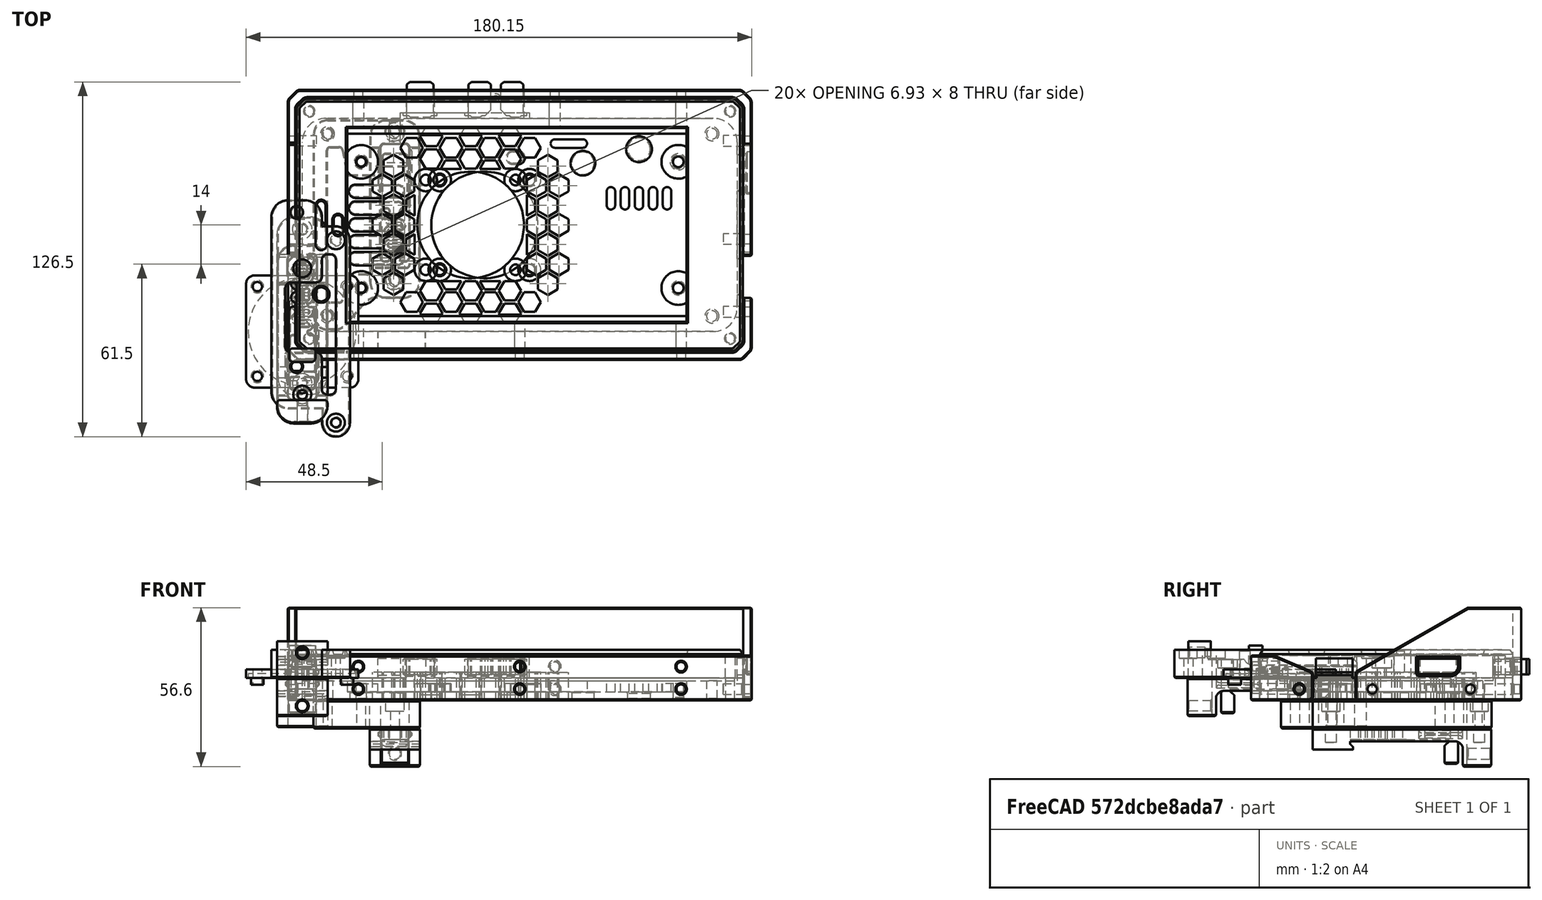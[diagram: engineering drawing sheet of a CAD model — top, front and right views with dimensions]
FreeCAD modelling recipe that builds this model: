
FCSTD DOCUMENT  (FreeCAD 0.19R24291 (Git))
Label: pixel-xl-navi-case-trim
License: Other
LicenseURL: GPL3
objects: Sketcher::SketchObject×56, PartDesign::Pocket×40, PartDesign::Chamfer×24, PartDesign::Pad×21, PartDesign::Fillet×18, Part::Box×16, PartDesign::Plane×12, Part::Feature×10, Part::MultiFuse×10, PartDesign::Body×9, Part::Chamfer×7, Part::Cylinder×6, Part::Cut×5, Part::Fillet×3, PartDesign::FeatureBase×2, Spreadsheet::Sheet×1, Mesh::Feature×1, Part::FeaturePython×1, Part::Extrusion×1
note: 344 computed .brp shape members not serialized (recipe doc carries the construction recipe); baked Part::Feature solids carry a one-line shape summary decoded from their .brp

FEATURE [Spreadsheet::Sheet] Spreadsheet  label="args"
  cells = A2=pixel width; B2(pixel_w)=155; A3=pixel heigh; B3(pixel_h)=76; A4=pixel thickness; B4(pixel_t)=8; A5=top screen offset; B5(screen_top_offset)=16; A6=bottom screen offset; B6(screen_bottom_offset)=17; A7=side screen offset; B7(screen_side_offset)=3.5; A8=power button offset; B8(button_power_offset)=37; A9=volume button offset; B9(button_volume_offset)=59; A10=power button width; B10(button_power_width)=10; A11=volume button width; B11(button_volume_width)=20; A12=screen width; B12(screen_width)=121; A13=screen heigh; B13(screen_heigh)=69; A14=pixel corner radius; B14(pixel_corner_radius)=8.5; A18=case thickness; B18(case_thickness)=10; A19=case width offset; B19(case_width_offset)=2; A20=case heigh offset; B20(case_heigh_offset)=7; A21=case corner radius; B21(case_corner_radius)=3; A23=front speaker offset; B23(front_speaker_offset)=5.75; A24=front speaker width; B24(front_speaker_width)=2; A25=front speaker heigh; B25(front_speaker_heigh)=16; A27=light sensor width; B27(light_sensor_width)=2; A28=light sensor heigh; B28(light_sensor_heigh)=6; A29=light sensor offset; B29(light_sensor_offset)=11.75; A31=camera x offset; B31(camera_x_offset)=6.75; A32=camera y offset; B32(camera_y_offset)=13.25; A33=camera radius; B33(camera_radius)=2; A35=speaker offset; B35(spekaer_offset)=14; A36=speaker width; B36(speaker_width)=11; A39=back thickness; B39(back_thickness)=8; A41=fan offset; B41(fan_offset)=65; C41=60; A43=wiring hole offset; B43(wiring_hole_offset)=120; A44=wiring hole radius; B44(wiring_hole_radius)=4; A46=sim slot offset; B46(sim_slot_offset)=28; A47=sim slot width; B47(sim_slot_width)=15; A49=headphone jack center offset; B49(headphone_jack_center_offset)=22; A50=headphone jack radius; B50(headphone_jack_radius)=5; A51=headphone_jack_width; B51(headphone_jack_width)=8; A53=sun visor heigh; B53(sun_visor_heigh)=15; A54=sun visor ramp width; B54(sun_visor_ramp_width)=40
FEATURE [Sketcher::SketchObject] Sketch
  FullyConstrained = true
  MapMode = 5
  Support = -> [XY_Plane]
  expr: Constraints[8] = <<args>>.case_heigh_offset
  expr: Constraints[9] = <<args>>.case_width_offset
  expr: Constraints[10] = <<args>>.pixel_h + <<args>>.case_heigh_offset
  expr: Constraints[11] = <<args>>.pixel_w + <<args>>.case_width_offset
  sketch-geometry (4):
    g0: LineSegment StartX=-2 StartY=-7 StartZ=0 EndX=157 EndY=-7 EndZ=0
    g1: LineSegment StartX=157 StartY=-7 StartZ=0 EndX=157 EndY=83 EndZ=0
    g2: LineSegment StartX=157 StartY=83 StartZ=0 EndX=-2 EndY=83 EndZ=0
    g3: LineSegment StartX=-2 StartY=83 StartZ=0 EndX=-2 EndY=-7 EndZ=0
  constraints (12):
    c: Coincident(g0,g1)
    c: Coincident(g1,g2)
    c: Coincident(g2,g3)
    c: Coincident(g3,g0)
    c: Horizontal(g0)
    c: Horizontal(g2)
    c: Vertical(g1)
    c: Vertical(g3)
    c: DistanceY(g0,g-1) = 7
    c: DistanceX(g0,g-1) = 2
    c: DistanceY(g-1,g2) = 83
    c: DistanceX(g-1,g1) = 157
FEATURE [PartDesign::Pad] Pad
  Direction = (1,1,1)
  Length = 10
  Length2 = 100
  Profile = -> Sketch
  Type = 0
  expr: Length = <<args>>.case_thickness
FEATURE [PartDesign::Plane] DatumPlane  label="face-plane"
  AttachmentOffset = pos=(0,0,10) rot=(0,0,1;0rad)
  Length = 210.04
  MapMode = 5
  Placement = pos=(0,0,10) rot=(0,0,1;0rad)
  ResizeMode = 0
  Support = -> [XY_Plane]
  Width = 136.04
  expr: .AttachmentOffset.Base.z = <<args>>.case_thickness
FEATURE [Sketcher::SketchObject] Sketch001
  FullyConstrained = true
  MapMode = 5
  Placement = pos=(0,0,10) rot=(0,0,1;0rad)
  Support = -> [DatumPlane]
  expr: Constraints[8] = <<args>>.screen_top_offset
  expr: Constraints[9] = <<args>>.screen_side_offset
  expr: Constraints[10] = <<args>>.screen_width
  expr: Constraints[11] = <<args>>.screen_heigh
  sketch-geometry (4):
    g0: LineSegment StartX=16 StartY=72.5 StartZ=0 EndX=137 EndY=72.5 EndZ=0
    g1: LineSegment StartX=137 StartY=72.5 StartZ=0 EndX=137 EndY=3.5 EndZ=0
    g2: LineSegment StartX=137 StartY=3.5 StartZ=0 EndX=16 EndY=3.5 EndZ=0
    g3: LineSegment StartX=16 StartY=3.5 StartZ=0 EndX=16 EndY=72.5 EndZ=0
  constraints (12):
    c: Coincident(g0,g1)
    c: Coincident(g1,g2)
    c: Coincident(g2,g3)
    c: Coincident(g3,g0)
    c: Horizontal(g0)
    c: Horizontal(g2)
    c: Vertical(g1)
    c: Vertical(g3)
    c: DistanceX(g-1,g2) = 16
    c: DistanceY(g-1,g2) = 3.5
    c: DistanceX(g0,g0) = 121
    c: DistanceY(g1,g1) = 69
FEATURE [PartDesign::Pocket] Pocket
  BaseFeature = -> Pad
  Length = 5
  Length2 = 100
  Profile = -> Sketch001
  Type = 1
FEATURE [PartDesign::Plane] DatumPlane001  label="zero-plane"
  Length = 210.04
  MapMode = 5
  ResizeMode = 0
  Support = -> [XY_Plane]
  Width = 136.04
FEATURE [Sketcher::SketchObject] Sketch002
  FullyConstrained = true
  MapMode = 5
  Support = -> [DatumPlane001]
  expr: Constraints[9] = <<args>>.pixel_w
  expr: Constraints[10] = <<args>>.pixel_h
  sketch-geometry (4):
    g0: LineSegment StartX=0 StartY=0 StartZ=0 EndX=155 EndY=0 EndZ=0
    g1: LineSegment StartX=155 StartY=0 StartZ=0 EndX=155 EndY=76 EndZ=0
    g2: LineSegment StartX=155 StartY=76 StartZ=0 EndX=0 EndY=76 EndZ=0
    g3: LineSegment StartX=0 StartY=76 StartZ=0 EndX=0 EndY=0 EndZ=0
  constraints (11):
    c: Coincident(g0,g1)
    c: Coincident(g1,g2)
    c: Coincident(g2,g3)
    c: Coincident(g3,g0)
    c: Horizontal(g0)
    c: Horizontal(g2)
    c: Vertical(g1)
    c: Vertical(g3)
    c: Coincident(g0,g-1)
    c: DistanceX(g2,g2) = 155
    c: DistanceY(g1,g1) = 76
FEATURE [PartDesign::Pocket] Pocket001
  BaseFeature = -> Pocket
  Length = 8
  Length2 = 100
  Profile = -> Sketch002
  Reversed = true
  Type = 0
  expr: Length = <<args>>.case_thickness - 2
FEATURE [Sketcher::SketchObject] Sketch003
  FullyConstrained = true
  MapMode = 5
  Placement = pos=(0,0,10) rot=(0,0,1;0rad)
  Support = -> [DatumPlane]
  expr: Constraints[12] = <<args>>.camera_radius + 0.5
  expr: Constraints[13] = <<args>>.camera_x_offset
  expr: Constraints[14] = <<args>>.camera_y_offset
  expr: Constraints[17] = <<args>>.front_speaker_heigh - <<args>>.front_speaker_width
  expr: Constraints[22] = (<<args>>.pixel_h - <<args>>.light_sensor_heigh) / 2 + <<args>>.light_sensor_width / 2
  expr: Constraints[15] = <<args>>.front_speaker_offset + <<args>>.front_speaker_width / 2
  expr: Constraints[20] = <<args>>.light_sensor_offset + <<args>>.light_sensor_width / 2
  expr: Constraints[16] = (<<args>>.pixel_h - <<args>>.front_speaker_heigh) / 2 + <<args>>.front_speaker_width / 2
  expr: Constraints[18] = <<args>>.front_speaker_width / 2 + 0.5
  expr: Constraints[19] = <<args>>.light_sensor_width / 2 + 0.5
  expr: Constraints[21] = <<args>>.light_sensor_heigh - <<args>>.light_sensor_width
  sketch-geometry (9):
    g0: ArcOfCircle CenterX=6.75 CenterY=45 CenterZ=0 NormalX=0 NormalY=0 NormalZ=1 AngleXU=0 Radius=1.5 StartAngle=2e-16 EndAngle=3.14159
    g1: ArcOfCircle CenterX=6.75 CenterY=31 CenterZ=0 NormalX=0 NormalY=0 NormalZ=1 AngleXU=0 Radius=1.5 StartAngle=3.14159 EndAngle=6.28319
    g2: LineSegment StartX=5.25 StartY=45 StartZ=0 EndX=5.25 EndY=31 EndZ=0
    g3: LineSegment StartX=8.25 StartY=45 StartZ=0 EndX=8.25 EndY=31 EndZ=0
    g4: ArcOfCircle CenterX=12.75 CenterY=40 CenterZ=0 NormalX=0 NormalY=0 NormalZ=1 AngleXU=0 Radius=1.5 StartAngle=2.4e-15 EndAngle=3.14159
    g5: ArcOfCircle CenterX=12.75 CenterY=36 CenterZ=0 NormalX=0 NormalY=0 NormalZ=1 AngleXU=0 Radius=1.5 StartAngle=3.14159 EndAngle=6.28319
    g6: LineSegment StartX=11.25 StartY=40 StartZ=0 EndX=11.25 EndY=36 EndZ=0
    g7: LineSegment StartX=14.25 StartY=40 StartZ=0 EndX=14.25 EndY=36 EndZ=0
    g8: Circle CenterX=6.75 CenterY=13.25 CenterZ=0 NormalX=0 NormalY=0 NormalZ=1 AngleXU=0 Radius=2.5
  constraints (23):
    c: Tangent(g0,g3) = 1.5708
    c: Tangent(g0,g2) = -1.5708
    c: Tangent(g2,g1) = -1.5708
    c: Tangent(g3,g1) = 1.5708
    c: Vertical(g2)
    c: Equal(g0,g1)
    c: Tangent(g4,g7) = 1.5708
    c: Tangent(g4,g6) = -1.5708
    c: Tangent(g6,g5) = -1.5708
    c: Tangent(g7,g5) = 1.5708
    c: Vertical(g6)
    c: Equal(g4,g5)
    c: Radius(g8) = 2.5
    c: DistanceX(g-1,g8) = 6.75
    c: DistanceY(g-1,g8) = 13.25
    c: DistanceX(g-1,g1) = 6.75
    c: DistanceY(g-1,g1) = 31
    c: DistanceY(g1,g0) = 14
    c: Radius(g0) = 1.5
    c: Radius(g4) = 1.5
    c: DistanceX(g-1,g5) = 12.75
    c: DistanceY(g5,g4) = 4
    c: DistanceY(g-1,g5) = 36
FEATURE [PartDesign::Pocket] Pocket002
  BaseFeature = -> Pocket001
  Length = 5
  Length2 = 100
  Profile = -> Sketch003
  Type = 1
FEATURE [PartDesign::Plane] DatumPlane002  label="right-edge-plane"
  AttachmentOffset = pos=(0,0,-83) rot=(0,0,1;0rad)
  Length = 201.079
  MapMode = 5
  Placement = pos=(0,83,1.84e-14) rot=(1,0,0;1.5708rad)
  ResizeMode = 0
  Support = -> [XZ_Plane]
  Width = 69.0788
  expr: .AttachmentOffset.Base.z = -(<<args>>.pixel_h + <<args>>.case_heigh_offset)
FEATURE [Sketcher::SketchObject] Sketch007
  FullyConstrained = true
  MapMode = 5
  Placement = pos=(0,83,1.84e-14) rot=(1,0,0;1.5708rad)
  Support = -> [DatumPlane002]
  expr: Constraints[19] = <<args>>.button_power_offset
  expr: Constraints[18] = <<args>>.button_volume_offset
  expr: Constraints[17] = <<args>>.button_volume_width
  expr: Constraints[16] = <<args>>.button_power_width
  sketch-geometry (8):
    g0: LineSegment StartX=37 StartY=7 StartZ=0 EndX=47 EndY=7 EndZ=0
    g1: LineSegment StartX=47 StartY=7 StartZ=0 EndX=47 EndY=0 EndZ=0
    g2: LineSegment StartX=47 StartY=0 StartZ=0 EndX=37 EndY=0 EndZ=0
    g3: LineSegment StartX=37 StartY=0 StartZ=0 EndX=37 EndY=7 EndZ=0
    g4: LineSegment StartX=59 StartY=7 StartZ=0 EndX=79 EndY=7 EndZ=0
    g5: LineSegment StartX=79 StartY=7 StartZ=0 EndX=79 EndY=0 EndZ=0
    g6: LineSegment StartX=79 StartY=0 StartZ=0 EndX=59 EndY=0 EndZ=0
    g7: LineSegment StartX=59 StartY=0 StartZ=0 EndX=59 EndY=7 EndZ=0
  constraints (24):
    c: Coincident(g0,g1)
    c: Coincident(g1,g2)
    c: Coincident(g2,g3)
    c: Coincident(g3,g0)
    c: Horizontal(g0)
    c: Horizontal(g2)
    c: Vertical(g1)
    c: Vertical(g3)
    c: Coincident(g4,g5)
    c: Coincident(g5,g6)
    c: Coincident(g6,g7)
    c: Coincident(g7,g4)
    c: Horizontal(g4)
    c: Horizontal(g6)
    c: Vertical(g5)
    c: Vertical(g7)
    c: DistanceX(g2,g2) = 10
    c: DistanceX(g6,g6) = 20
    c: DistanceX(g-1,g6) = 59
    c: DistanceX(g-1,g2) = 37
    c: DistanceY(g-1,g2) = 0
    c: DistanceY(g-1,g6) = 0
    c: DistanceY(g3,g3) = 7
    c: DistanceY(g7,g7) = 7
FEATURE [PartDesign::Plane] DatumPlane003  label="bottom-edge-plane"
  AttachmentOffset = pos=(0,0,157) rot=(0,0,1;0rad)
  Length = 122.697
  MapMode = 5
  Placement = pos=(157,-3.49e-14,3.49e-14) rot=(0.57735,0.57735,0.57735;2.0944rad)
  ResizeMode = 0
  Support = -> [YZ_Plane]
  Width = 64.6969
  expr: .AttachmentOffset.Base.z = <<args>>.pixel_w + <<args>>.case_width_offset
FEATURE [Sketcher::SketchObject] Sketch008
  FullyConstrained = true
  MapMode = 5
  Placement = pos=(157,-3.49e-14,3.49e-14) rot=(0.57735,0.57735,0.57735;2.0944rad)
  Support = -> [DatumPlane003]
  expr: Constraints[20] = <<args>>.spekaer_offset - 1
  expr: Constraints[23] = <<args>>.pixel_h - (<<args>>.spekaer_offset + <<args>>.speaker_width + 2 - 1)
  expr: Constraints[19] = <<args>>.speaker_width + 2
  expr: Constraints[18] = <<args>>.speaker_width + 2
  sketch-geometry (8):
    g0: LineSegment StartX=13 StartY=0 StartZ=0 EndX=26 EndY=0 EndZ=0
    g1: LineSegment StartX=26 StartY=0 StartZ=0 EndX=26 EndY=7 EndZ=0
    g2: LineSegment StartX=26 StartY=7 StartZ=0 EndX=13 EndY=7 EndZ=0
    g3: LineSegment StartX=13 StartY=7 StartZ=0 EndX=13 EndY=0 EndZ=0
    g4: LineSegment StartX=50 StartY=0 StartZ=0 EndX=63 EndY=0 EndZ=0
    g5: LineSegment StartX=63 StartY=0 StartZ=0 EndX=63 EndY=7 EndZ=0
    g6: LineSegment StartX=63 StartY=7 StartZ=0 EndX=50 EndY=7 EndZ=0
    g7: LineSegment StartX=50 StartY=7 StartZ=0 EndX=50 EndY=0 EndZ=0
  constraints (24):
    c: Coincident(g0,g1)
    c: Coincident(g1,g2)
    c: Coincident(g2,g3)
    c: Coincident(g3,g0)
    c: Horizontal(g0)
    c: Horizontal(g2)
    c: Vertical(g1)
    c: Vertical(g3)
    c: Coincident(g4,g5)
    c: Coincident(g5,g6)
    c: Coincident(g6,g7)
    c: Coincident(g7,g4)
    c: Horizontal(g4)
    c: Horizontal(g6)
    c: Vertical(g5)
    c: Vertical(g7)
    c: DistanceY(g-1,g0) = 0
    c: DistanceY(g-1,g4) = 0
    c: DistanceX(g2,g2) = 13
    c: DistanceX(g6,g6) = 13
    c: DistanceX(g-1,g0) = 13
    c: DistanceY(g1,g1) = 7
    c: DistanceY(g7,g7) = 7
    c: DistanceX(g-1,g4) = 50
FEATURE [Mesh::Feature] PixelXL
  Placement = pos=(77,38,8) rot=(0.707107,-0.707107,0;3.14159rad)
FEATURE [PartDesign::Plane] DatumPlane004  label="left-edge-plane"
  AttachmentOffset = pos=(0,0,7) rot=(0,0,1;0rad)
  Length = 201.079
  MapMode = 5
  Placement = pos=(0,-7,-1.6e-15) rot=(1,0,0;1.5708rad)
  ResizeMode = 0
  Support = -> [XZ_Plane]
  Width = 69.0788
  expr: .AttachmentOffset.Base.z = <<args>>.case_heigh_offset
FEATURE [Sketcher::SketchObject] Sketch009
  FullyConstrained = true
  MapMode = 5
  Placement = pos=(0,-7,-1.6e-15) rot=(1,0,0;1.5708rad)
  Support = -> [DatumPlane004]
  expr: Constraints[10] = <<args>>.pixel_t - 1
  expr: Constraints[9] = <<args>>.sim_slot_width + 2
  expr: Constraints[8] = <<args>>.sim_slot_offset - 1
  sketch-geometry (4):
    g0: LineSegment StartX=27 StartY=7 StartZ=0 EndX=44 EndY=7 EndZ=0
    g1: LineSegment StartX=44 StartY=7 StartZ=0 EndX=44 EndY=0 EndZ=0
    g2: LineSegment StartX=44 StartY=0 StartZ=0 EndX=27 EndY=0 EndZ=0
    g3: LineSegment StartX=27 StartY=0 StartZ=0 EndX=27 EndY=7 EndZ=0
  constraints (12):
    c: Coincident(g0,g1)
    c: Coincident(g1,g2)
    c: Coincident(g2,g3)
    c: Coincident(g3,g0)
    c: Horizontal(g0)
    c: Horizontal(g2)
    c: Vertical(g1)
    c: Vertical(g3)
    c: DistanceX(g-1,g2) = 27
    c: DistanceX(g0,g0) = 17
    c: DistanceY(g1,g1) = 7
    c: DistanceY(g-1,g2) = 0
FEATURE [PartDesign::Plane] DatumPlane005  label="top-edge-plane"
  AttachmentOffset = pos=(0,0,-7) rot=(0,0,1;0rad)
  Length = 122.697
  MapMode = 5
  Placement = pos=(-7,1.6e-15,-1.6e-15) rot=(0.57735,0.57735,0.57735;2.0944rad)
  ResizeMode = 0
  Support = -> [YZ_Plane]
  Width = 64.6969
  expr: .AttachmentOffset.Base.z = -<<args>>.case_heigh_offset
FEATURE [Sketcher::SketchObject] Sketch010
  FullyConstrained = true
  MapMode = 5
  Placement = pos=(-7,1.6e-15,-1.6e-15) rot=(0.57735,0.57735,0.57735;2.0944rad)
  Support = -> [DatumPlane005]
  expr: Constraints[10] = <<args>>.pixel_t
  expr: Constraints[9] = <<args>>.headphone_jack_width
  expr: Constraints[8] = <<args>>.headphone_jack_center_offset - <<args>>.headphone_jack_width / 2
  sketch-geometry (4):
    g0: LineSegment StartX=18 StartY=8 StartZ=0 EndX=26 EndY=8 EndZ=0
    g1: LineSegment StartX=26 StartY=8 StartZ=0 EndX=26 EndY=0 EndZ=0
    g2: LineSegment StartX=26 StartY=0 StartZ=0 EndX=18 EndY=0 EndZ=0
    g3: LineSegment StartX=18 StartY=0 StartZ=0 EndX=18 EndY=8 EndZ=0
  constraints (12):
    c: Coincident(g0,g1)
    c: Coincident(g1,g2)
    c: Coincident(g2,g3)
    c: Coincident(g3,g0)
    c: Horizontal(g0)
    c: Horizontal(g2)
    c: Vertical(g1)
    c: Vertical(g3)
    c: DistanceX(g-1,g2) = 18
    c: DistanceX(g2,g2) = 8
    c: DistanceY(g3,g3) = 8
    c: DistanceY(g-1,g2) = 0
FEATURE [PartDesign::Plane] DatumPlane006  label="zero-plane001"
  Length = 210.04
  MapMode = 5
  ResizeMode = 0
  Support = -> [XY_Plane001]
  Width = 136.04
FEATURE [Sketcher::SketchObject] Sketch011
  FullyConstrained = true
  MapMode = 5
  Support = -> [DatumPlane006]
  expr: Constraints[8] = <<args>>.case_width_offset * 2 + <<args>>.pixel_w
  expr: Constraints[9] = <<args>>.case_heigh_offset * 2 + <<args>>.pixel_h
  expr: Constraints[10] = <<args>>.case_width_offset
  expr: Constraints[11] = <<args>>.case_heigh_offset
  sketch-geometry (4):
    g0: LineSegment StartX=-2 StartY=-7 StartZ=0 EndX=157 EndY=-7 EndZ=0
    g1: LineSegment StartX=157 StartY=-7 StartZ=0 EndX=157 EndY=83 EndZ=0
    g2: LineSegment StartX=157 StartY=83 StartZ=0 EndX=-2 EndY=83 EndZ=0
    g3: LineSegment StartX=-2 StartY=83 StartZ=0 EndX=-2 EndY=-7 EndZ=0
  constraints (12):
    c: Coincident(g0,g1)
    c: Coincident(g1,g2)
    c: Coincident(g2,g3)
    c: Coincident(g3,g0)
    c: Horizontal(g0)
    c: Horizontal(g2)
    c: Vertical(g1)
    c: Vertical(g3)
    c: DistanceX(g2,g2) = 159
    c: DistanceY(g1,g1) = 90
    c: DistanceX(g0,g-1) = 2
    c: DistanceY(g0,g-1) = 7
FEATURE [PartDesign::Pad] Pad001
  Direction = (1,1,1)
  Length = 8
  Length2 = 100
  Profile = -> Sketch011
  Type = 0
  expr: Length = <<args>>.back_thickness
FEATURE [PartDesign::Plane] DatumPlane007  label="inner-face-plane"
  AttachmentOffset = pos=(0,0,8) rot=(0,0,1;0rad)
  Length = 210.04
  MapMode = 5
  Placement = pos=(0,0,8) rot=(0,0,1;0rad)
  ResizeMode = 0
  Support = -> [XY_Plane001]
  Width = 136.04
  expr: .AttachmentOffset.Base.z = <<args>>.back_thickness
FEATURE [Sketcher::SketchObject] Sketch012
  FullyConstrained = true
  MapMode = 5
  Placement = pos=(0,0,8) rot=(0,0,1;0rad)
  Support = -> [DatumPlane007]
  expr: Constraints[8] = <<args>>.screen_heigh - 4
  expr: Constraints[9] = <<args>>.screen_width
  expr: Constraints[10] = <<args>>.screen_side_offset + 2
  expr: Constraints[11] = <<args>>.screen_top_offset
  sketch-geometry (4):
    g0: LineSegment StartX=16 StartY=5.5 StartZ=0 EndX=137 EndY=5.5 EndZ=0
    g1: LineSegment StartX=137 StartY=5.5 StartZ=0 EndX=137 EndY=70.5 EndZ=0
    g2: LineSegment StartX=137 StartY=70.5 StartZ=0 EndX=16 EndY=70.5 EndZ=0
    g3: LineSegment StartX=16 StartY=70.5 StartZ=0 EndX=16 EndY=5.5 EndZ=0
  constraints (12):
    c: Coincident(g0,g1)
    c: Coincident(g1,g2)
    c: Coincident(g2,g3)
    c: Coincident(g3,g0)
    c: Horizontal(g0)
    c: Horizontal(g2)
    c: Vertical(g1)
    c: Vertical(g3)
    c: DistanceY(g1,g1) = 65
    c: DistanceX(g2,g2) = 121
    c: DistanceY(g-1,g0) = 5.5
    c: DistanceX(g-1,g0) = 16
FEATURE [PartDesign::Pocket] Pocket009
  BaseFeature = -> Pad001
  Length = 5
  Length2 = 100
  Profile = -> Sketch012
  Type = 0
FEATURE [PartDesign::Plane] DatumPlane009  label="left-edge-plane001"
  AttachmentOffset = pos=(0,0,7) rot=(0,0,1;0rad)
  Length = 201.079
  MapMode = 5
  Placement = pos=(0,-7,-1.6e-15) rot=(1,0,0;1.5708rad)
  ResizeMode = 0
  Support = -> [XZ_Plane001]
  Width = 69.0788
  expr: .AttachmentOffset.Base.z = <<args>>.case_heigh_offset
FEATURE [PartDesign::Plane] DatumPlane010  label="top-edge-plane001"
  AttachmentOffset = pos=(0,0,-2) rot=(0,0,1;0rad)
  Length = 122.697
  MapMode = 5
  Placement = pos=(-2,4e-16,-4e-16) rot=(0.57735,0.57735,0.57735;2.0944rad)
  ResizeMode = 0
  Support = -> [YZ_Plane001]
  Width = 64.6969
  expr: .AttachmentOffset.Base.z = -<<args>>.case_width_offset
FEATURE [PartDesign::Plane] DatumPlane011  label="bottom-edge-plane001"
  AttachmentOffset = pos=(0,0,157) rot=(0,0,1;0rad)
  Length = 122.697
  MapMode = 5
  Placement = pos=(157,-3.49e-14,3.49e-14) rot=(0.57735,0.57735,0.57735;2.0944rad)
  ResizeMode = 0
  Support = -> [YZ_Plane001]
  Width = 64.6969
  expr: .AttachmentOffset.Base.z = <<args>>.pixel_w + <<args>>.case_width_offset
FEATURE [PartDesign::Plane] DatumPlane012  label="right-edge-plane001"
  AttachmentOffset = pos=(0,0,-83) rot=(0,0,1;0rad)
  Length = 201.079
  MapMode = 5
  Placement = pos=(0,83,1.84e-14) rot=(1,0,0;1.5708rad)
  ResizeMode = 0
  Support = -> [XZ_Plane001]
  Width = 69.0788
  expr: .AttachmentOffset.Base.z = -(<<args>>.pixel_h + <<args>>.case_heigh_offset)
FEATURE [Sketcher::SketchObject] Sketch013
  FullyConstrained = true
  MapMode = 5
  Placement = pos=(0,83,1.84e-14) rot=(1,0,0;1.5708rad)
  Support = -> [DatumPlane012]
  expr: Constraints[16] = <<args>>.back_thickness
  expr: Constraints[17] = <<args>>.back_thickness
  expr: Constraints[22] = <<args>>.button_power_offset + 0.15
  expr: Constraints[20] = <<args>>.button_power_width - 0.3
  expr: Constraints[21] = <<args>>.button_volume_width - 0.3
  expr: Constraints[23] = <<args>>.button_volume_offset + 0.15
  sketch-geometry (8):
    g0: LineSegment StartX=37.15 StartY=9 StartZ=0 EndX=46.85 EndY=9 EndZ=0
    g1: LineSegment StartX=46.85 StartY=9 StartZ=0 EndX=46.85 EndY=8 EndZ=0
    g2: LineSegment StartX=46.85 StartY=8 StartZ=0 EndX=37.15 EndY=8 EndZ=0
    g3: LineSegment StartX=37.15 StartY=8 StartZ=0 EndX=37.15 EndY=9 EndZ=0
    g4: LineSegment StartX=59.15 StartY=9 StartZ=0 EndX=78.85 EndY=9 EndZ=0
    g5: LineSegment StartX=78.85 StartY=9 StartZ=0 EndX=78.85 EndY=8 EndZ=0
    g6: LineSegment StartX=78.85 StartY=8 StartZ=0 EndX=59.15 EndY=8 EndZ=0
    g7: LineSegment StartX=59.15 StartY=8 StartZ=0 EndX=59.15 EndY=9 EndZ=0
  constraints (24):
    c: Coincident(g0,g1)
    c: Coincident(g1,g2)
    c: Coincident(g2,g3)
    c: Coincident(g3,g0)
    c: Horizontal(g0)
    c: Horizontal(g2)
    c: Vertical(g1)
    c: Vertical(g3)
    c: Coincident(g4,g5)
    c: Coincident(g5,g6)
    c: Coincident(g6,g7)
    c: Coincident(g7,g4)
    c: Horizontal(g4)
    c: Horizontal(g6)
    c: Vertical(g5)
    c: Vertical(g7)
    c: DistanceY(g-1,g2) = 8
    c: DistanceY(g-1,g6) = 8
    c: DistanceY(g3,g3) = 1
    c: DistanceY(g7,g7) = 1
    c: DistanceX(g0,g0) = 9.7
    c: DistanceX(g4,g4) = 19.7
    c: DistanceX(g-1,g2) = 37.15
    c: DistanceX(g-1,g6) = 59.15
FEATURE [PartDesign::Pad] Pad002  label="right-pad"
  BaseFeature = -> Pocket009
  Direction = (1,1,1)
  Length = 7
  Length2 = 100
  Profile = -> Sketch013
  Type = 0
  expr: Length = <<args>>.case_heigh_offset
FEATURE [Sketcher::SketchObject] Sketch014
  FullyConstrained = true
  MapMode = 5
  Placement = pos=(157,-3.49e-14,3.49e-14) rot=(0.57735,0.57735,0.57735;2.0944rad)
  Support = -> [DatumPlane011]
  expr: Constraints[16] = <<args>>.speaker_width - 0.3 + 2
  expr: Constraints[17] = <<args>>.speaker_width - 0.3 + 2
  expr: Constraints[22] = <<args>>.spekaer_offset + 0.15 - 1
  expr: Constraints[18] = <<args>>.back_thickness
  expr: Constraints[19] = <<args>>.back_thickness
  expr: Constraints[23] = <<args>>.pixel_h - (<<args>>.spekaer_offset + <<args>>.speaker_width + 2 - 1) + 0.15
  sketch-geometry (8):
    g0: LineSegment StartX=13.15 StartY=9 StartZ=0 EndX=25.85 EndY=9 EndZ=0
    g1: LineSegment StartX=25.85 StartY=9 StartZ=0 EndX=25.85 EndY=8 EndZ=0
    g2: LineSegment StartX=25.85 StartY=8 StartZ=0 EndX=13.15 EndY=8 EndZ=0
    g3: LineSegment StartX=13.15 StartY=8 StartZ=0 EndX=13.15 EndY=9 EndZ=0
    g4: LineSegment StartX=50.15 StartY=9 StartZ=0 EndX=62.85 EndY=9 EndZ=0
    g5: LineSegment StartX=62.85 StartY=9 StartZ=0 EndX=62.85 EndY=8 EndZ=0
    g6: LineSegment StartX=62.85 StartY=8 StartZ=0 EndX=50.15 EndY=8 EndZ=0
    g7: LineSegment StartX=50.15 StartY=8 StartZ=0 EndX=50.15 EndY=9 EndZ=0
  constraints (24):
    c: Coincident(g0,g1)
    c: Coincident(g1,g2)
    c: Coincident(g2,g3)
    c: Coincident(g3,g0)
    c: Horizontal(g0)
    c: Horizontal(g2)
    c: Vertical(g1)
    c: Vertical(g3)
    c: Coincident(g4,g5)
    c: Coincident(g5,g6)
    c: Coincident(g6,g7)
    c: Coincident(g7,g4)
    c: Horizontal(g4)
    c: Horizontal(g6)
    c: Vertical(g5)
    c: Vertical(g7)
    c: DistanceX(g0,g0) = 12.7
    c: DistanceX(g4,g4) = 12.7
    c: DistanceY(g-1,g2) = 8
    c: DistanceY(g-1,g6) = 8
    c: DistanceY(g3,g3) = 1
    c: DistanceY(g7,g7) = 1
    c: DistanceX(g-1,g2) = 13.15
    c: DistanceX(g-1,g6) = 50.15
FEATURE [PartDesign::Pad] Pad003  label="bottom-pad"
  BaseFeature = -> Pad002
  Direction = (1,1,1)
  Length = 2
  Length2 = 100
  Profile = -> Sketch014
  Reversed = true
  Type = 0
  expr: Length = <<args>>.case_width_offset
FEATURE [Sketcher::SketchObject] Sketch015
  FullyConstrained = true
  MapMode = 5
  Support = -> [DatumPlane001]
  expr: Constraints[7] = <<args>>.pixel_h + 2.5
  expr: Constraints[8] = <<args>>.pixel_h + 2.5
  expr: Constraints[10] = <<args>>.pixel_w - 2.5
  expr: Constraints[11] = <<args>>.pixel_w - 2.5
  sketch-geometry (4):
    g0: Circle CenterX=2.5 CenterY=-2.5 CenterZ=0 NormalX=0 NormalY=0 NormalZ=1 AngleXU=0 Radius=1.9
    g1: Circle CenterX=2.5 CenterY=78.5 CenterZ=0 NormalX=0 NormalY=0 NormalZ=1 AngleXU=0 Radius=1.9
    g2: Circle CenterX=152.5 CenterY=78.5 CenterZ=0 NormalX=0 NormalY=0 NormalZ=1 AngleXU=0 Radius=1.9
    g3: Circle CenterX=152.5 CenterY=-2.5 CenterZ=0 NormalX=0 NormalY=0 NormalZ=1 AngleXU=0 Radius=1.9
  constraints (12):
    c: Radius(g2) = 1.9
    c: Radius(g3) = 1.9
    c: Radius(g1) = 1.9
    c: Radius(g0) = 1.9
    c: DistanceY(g0,g-1) = 2.5
    c: DistanceX(g0,g-1) = -2.5
    c: DistanceX(g1,g-1) = -2.5
    c: DistanceY(g-1,g1) = 78.5
    c: DistanceY(g-1,g2) = 78.5
    c: DistanceY(g3,g0) = 0
    c: DistanceX(g-1,g2) = 152.5
    c: DistanceX(g-1,g3) = 152.5
FEATURE [Sketcher::SketchObject] Sketch016
  FullyConstrained = true
  MapMode = 5
  Support = -> [DatumPlane006]
  expr: Constraints[6] = <<args>>.pixel_h + 2.5
  expr: Constraints[7] = <<args>>.pixel_h + 2.5
  expr: Constraints[10] = <<args>>.pixel_w - 2.5
  expr: Constraints[11] = <<args>>.pixel_w - 2.5 * 2
  sketch-geometry (4):
    g0: Circle CenterX=2.5 CenterY=78.5 CenterZ=0 NormalX=0 NormalY=0 NormalZ=1 AngleXU=0 Radius=1.65
    g1: Circle CenterX=152.5 CenterY=78.5 CenterZ=0 NormalX=0 NormalY=0 NormalZ=1 AngleXU=0 Radius=1.65
    g2: Circle CenterX=152.5 CenterY=-2.5 CenterZ=0 NormalX=0 NormalY=0 NormalZ=1 AngleXU=0 Radius=1.65
    g3: Circle CenterX=2.5 CenterY=-2.5 CenterZ=0 NormalX=0 NormalY=0 NormalZ=1 AngleXU=0 Radius=1.65
  constraints (12):
    c: Radius(g3) = 1.65
    c: Radius(g0) = 1.65
    c: Radius(g1) = 1.65
    c: Radius(g2) = 1.65
    c: DistanceY(g3,g-1) = 2.5
    c: DistanceY(g2,g-1) = 2.5
    c: DistanceY(g-1,g0) = 78.5
    c: DistanceY(g-1,g1) = 78.5
    c: DistanceX(g0,g-1) = -2.5
    c: DistanceX(g-1,g3) = 2.5
    c: DistanceX(g-1,g2) = 152.5
    c: DistanceX(g0,g1) = 150
FEATURE [PartDesign::Pocket] Pocket011
  BaseFeature = -> Pad003
  Length = 5
  Length2 = 100
  Profile = -> Sketch016
  Reversed = true
  Type = 1
FEATURE [Part::Feature] Cut001001  label="hex-cut"
  Placement = pos=(70,58,0) rot=(0,0,1;0rad)
FEATURE [Part::Feature] Cut001002  label="hex-cut001"
  Placement = pos=(70,18,0) rot=(0,0,1;3.14159rad)
FEATURE [Part::Feature] Cut001003  label="hex-cut002"
  Placement = pos=(50,38,0) rot=(0,0,1;1.5708rad)
FEATURE [Part::Feature] Cut001004  label="hex-cut003"
  Placement = pos=(90,38,0) rot=(0,0,-1;1.5708rad)
FEATURE [Sketcher::SketchObject] Sketch017
  FullyConstrained = true
  MapMode = 5
  Support = -> [DatumPlane006]
  expr: Constraints[0] = <<args>>.pixel_h / 2
  expr: Constraints[2] = <<args>>.fan_offset
  sketch-geometry (5):
    g0: Circle CenterX=65 CenterY=38 CenterZ=0 NormalX=0 NormalY=0 NormalZ=1 AngleXU=0 Radius=19
    g1: Circle CenterX=49 CenterY=54 CenterZ=0 NormalX=0 NormalY=0 NormalZ=1 AngleXU=0 Radius=1.9
    g2: Circle CenterX=81 CenterY=54 CenterZ=0 NormalX=0 NormalY=0 NormalZ=1 AngleXU=0 Radius=1.9
    g3: Circle CenterX=81 CenterY=22 CenterZ=0 NormalX=0 NormalY=0 NormalZ=1 AngleXU=0 Radius=1.9
    g4: Circle CenterX=49 CenterY=22 CenterZ=0 NormalX=0 NormalY=0 NormalZ=1 AngleXU=0 Radius=1.9
  constraints (15):
    c: DistanceY(g-1,g0) = 38
    c: Radius(g0) = 19
    c: DistanceX(g-1,g0) = 65
    c: Vertical(g4,g1)
    c: Vertical(g2,g3)
    c: Horizontal(g1,g2)
    c: DistanceX(g1,g0) = 16
    c: DistanceX(g1,g2) = 32
    c: DistanceY(g0,g2) = 16
    c: DistanceY(g3,g2) = 32
    c: Horizontal(g4,g3)
    c: Radius(g1) = 1.9
    c: Radius(g2) = 1.9
    c: Radius(g4) = 1.9
    c: Radius(g3) = 1.9
FEATURE [PartDesign::Pocket] Pocket012
  BaseFeature = -> Pocket011
  Length = 5
  Length2 = 100
  Profile = -> Sketch017
  Reversed = true
  Type = 1
FEATURE [Sketcher::SketchObject] Sketch020
  FullyConstrained = true
  MapMode = 5
  Placement = pos=(0,0,8) rot=(0,0,1;0rad)
  Support = -> [DatumPlane007]
  expr: Constraints[8] = <<args>>.pixel_w
  expr: Constraints[9] = <<args>>.pixel_h
  sketch-geometry (4):
    g0: LineSegment StartX=0 StartY=76 StartZ=0 EndX=155 EndY=76 EndZ=0
    g1: LineSegment StartX=155 StartY=76 StartZ=0 EndX=155 EndY=0 EndZ=0
    g2: LineSegment StartX=155 StartY=0 StartZ=0 EndX=0 EndY=0 EndZ=0
    g3: LineSegment StartX=0 StartY=0 StartZ=0 EndX=0 EndY=76 EndZ=0
  constraints (12):
    c: Coincident(g0,g1)
    c: Coincident(g1,g2)
    c: Coincident(g2,g3)
    c: Coincident(g3,g0)
    c: Horizontal(g0)
    c: Horizontal(g2)
    c: Vertical(g1)
    c: Vertical(g3)
    c: DistanceX(g0,g0) = 155
    c: DistanceY(g1,g1) = 76
    c: DistanceX(g-1,g2) = 0
    c: DistanceY(g-1,g2) = 0
FEATURE [PartDesign::Pocket] Pocket015
  BaseFeature = -> Pocket012
  Length = 1
  Length2 = 100
  Profile = -> Sketch020
  Type = 0
FEATURE [Sketcher::SketchObject] Sketch021
  FullyConstrained = true
  MapMode = 5
  Placement = pos=(0,-7,-1.6e-15) rot=(1,0,0;1.5708rad)
  Support = -> [DatumPlane009]
  expr: Constraints[8] = <<args>>.back_thickness
  expr: Constraints[9] = <<args>>.sim_slot_offset + 0.15 - 1
  expr: Constraints[10] = <<args>>.sim_slot_width - 0.3 + 2
  sketch-geometry (4):
    g0: LineSegment StartX=27.15 StartY=9 StartZ=0 EndX=43.85 EndY=9 EndZ=0
    g1: LineSegment StartX=43.85 StartY=9 StartZ=0 EndX=43.85 EndY=8 EndZ=0
    g2: LineSegment StartX=43.85 StartY=8 StartZ=0 EndX=27.15 EndY=8 EndZ=0
    g3: LineSegment StartX=27.15 StartY=8 StartZ=0 EndX=27.15 EndY=9 EndZ=0
  constraints (12):
    c: Coincident(g0,g1)
    c: Coincident(g1,g2)
    c: Coincident(g2,g3)
    c: Coincident(g3,g0)
    c: Horizontal(g0)
    c: Horizontal(g2)
    c: Vertical(g1)
    c: Vertical(g3)
    c: DistanceY(g-1,g2) = 8
    c: DistanceX(g-1,g2) = 27.15
    c: DistanceX(g0,g0) = 16.7
    c: DistanceY(g1,g1) = 1
FEATURE [PartDesign::Pad] Pad004
  BaseFeature = -> Pocket015
  Direction = (1,1,1)
  Length = 7
  Length2 = 100
  Profile = -> Sketch021
  Reversed = true
  Type = 0
  expr: Length = <<args>>.case_heigh_offset
FEATURE [Part::Feature] Body004012  label="din-mount-template"
  Placement = pos=(0,10,-1e-15) rot=(0,1,0;3.14159rad)
FEATURE [Part::Feature] Body004013  label="din-mount-template001"
  Placement = pos=(120,26,-8) rot=(0,0,1;0rad)
FEATURE [Sketcher::SketchObject] Sketch023
  FullyConstrained = true
  MapMode = 5
  Placement = pos=(0,0,8) rot=(0,0,1;0rad)
  Support = -> [DatumPlane007]
  expr: Constraints[0] = <<args>>.wiring_hole_offset
  expr: Constraints[1] = <<args>>.pixel_h - <<args>>.wiring_hole_radius - 7
  expr: Constraints[2] = <<args>>.wiring_hole_radius
  sketch-geometry (1):
    g0: Circle CenterX=120 CenterY=65 CenterZ=0 NormalX=0 NormalY=0 NormalZ=1 AngleXU=0 Radius=4
  constraints (3):
    c: DistanceX(g-1,g0) = 120
    c: DistanceY(g-1,g0) = 65
    c: Radius(g0) = 4
FEATURE [PartDesign::Pocket] Pocket017
  BaseFeature = -> Pad004
  Length = 5
  Length2 = 100
  Profile = -> Sketch023
  Type = 1
FEATURE [Sketcher::SketchObject] Sketch024
  FullyConstrained = true
  MapMode = 5
  Support = -> [DatumPlane006]
  expr: Constraints[38] = <<args>>.wiring_hole_offset
  expr: Constraints[49] = <<args>>.pixel_h - <<args>>.wiring_hole_radius - 27
  sketch-geometry (20):
    g0: ArcOfCircle CenterX=115 CenterY=50 CenterZ=0 NormalX=0 NormalY=0 NormalZ=1 AngleXU=0 Radius=1.5 StartAngle=-9e-16 EndAngle=3.14159
    g1: ArcOfCircle CenterX=115 CenterY=45 CenterZ=0 NormalX=0 NormalY=0 NormalZ=1 AngleXU=0 Radius=1.5 StartAngle=3.14159 EndAngle=6.28319
    g2: LineSegment StartX=113.5 StartY=50 StartZ=0 EndX=113.5 EndY=45 EndZ=0
    g3: LineSegment StartX=116.5 StartY=50 StartZ=0 EndX=116.5 EndY=45 EndZ=0
    g4: ArcOfCircle CenterX=110 CenterY=50 CenterZ=0 NormalX=0 NormalY=0 NormalZ=1 AngleXU=0 Radius=1.5 StartAngle=-9e-16 EndAngle=3.14159
    g5: ArcOfCircle CenterX=110 CenterY=45 CenterZ=0 NormalX=0 NormalY=0 NormalZ=1 AngleXU=0 Radius=1.5 StartAngle=3.14159 EndAngle=6.28319
    g6: LineSegment StartX=108.5 StartY=50 StartZ=0 EndX=108.5 EndY=45 EndZ=0
    g7: LineSegment StartX=111.5 StartY=50 StartZ=0 EndX=111.5 EndY=45 EndZ=0
    g8: ArcOfCircle CenterX=125 CenterY=50 CenterZ=0 NormalX=0 NormalY=0 NormalZ=1 AngleXU=0 Radius=1.5 StartAngle=-1.8e-15 EndAngle=3.14159
    g9: ArcOfCircle CenterX=125 CenterY=45 CenterZ=0 NormalX=0 NormalY=0 NormalZ=1 AngleXU=0 Radius=1.5 StartAngle=3.14159 EndAngle=6.28319
    g10: LineSegment StartX=123.5 StartY=50 StartZ=0 EndX=123.5 EndY=45 EndZ=0
    g11: LineSegment StartX=126.5 StartY=50 StartZ=0 EndX=126.5 EndY=45 EndZ=0
    g12: ArcOfCircle CenterX=130 CenterY=50 CenterZ=0 NormalX=0 NormalY=0 NormalZ=1 AngleXU=0 Radius=1.5 StartAngle=-1.8e-15 EndAngle=3.14159
    g13: ArcOfCircle CenterX=130 CenterY=45 CenterZ=0 NormalX=0 NormalY=0 NormalZ=1 AngleXU=0 Radius=1.5 StartAngle=3.14159 EndAngle=6.28319
    g14: LineSegment StartX=128.5 StartY=50 StartZ=0 EndX=128.5 EndY=45 EndZ=0
    g15: LineSegment StartX=131.5 StartY=50 StartZ=0 EndX=131.5 EndY=45 EndZ=0
    g16: ArcOfCircle CenterX=120 CenterY=50 CenterZ=0 NormalX=0 NormalY=0 NormalZ=1 AngleXU=0 Radius=1.5 StartAngle=5.821e-13 EndAngle=3.14159
    g17: ArcOfCircle CenterX=120 CenterY=45 CenterZ=0 NormalX=0 NormalY=0 NormalZ=1 AngleXU=0 Radius=1.5 StartAngle=3.14159 EndAngle=6.28319
    g18: LineSegment StartX=118.5 StartY=50 StartZ=0 EndX=118.5 EndY=45 EndZ=0
    g19: LineSegment StartX=121.5 StartY=50 StartZ=0 EndX=121.5 EndY=45 EndZ=0
  constraints (50):
    c: Tangent(g0,g3) = 1.5708
    c: Tangent(g0,g2) = -1.5708
    c: Tangent(g2,g1) = -1.5708
    c: Tangent(g3,g1) = 1.5708
    c: Vertical(g2)
    c: Equal(g0,g1)
    c: Tangent(g4,g7) = 1.5708
    c: Tangent(g4,g6) = -1.5708
    c: Tangent(g6,g5) = -1.5708
    c: Tangent(g7,g5) = 1.5708
    c: Vertical(g6)
    c: Equal(g4,g5)
    c: Tangent(g8,g11) = 1.5708
    c: Tangent(g8,g10) = -1.5708
    c: Tangent(g10,g9) = -1.5708
    c: Tangent(g11,g9) = 1.5708
    c: Vertical(g10)
    c: Equal(g8,g9)
    c: Tangent(g12,g15) = 1.5708
    c: Tangent(g12,g14) = -1.5708
    c: Tangent(g14,g13) = -1.5708
    c: Tangent(g15,g13) = 1.5708
    c: Vertical(g14)
    c: Equal(g12,g13)
    c: Tangent(g16,g19) = 1.5708
    c: Tangent(g16,g18) = -1.5708
    c: Tangent(g18,g17) = -1.5708
    c: Tangent(g19,g17) = 1.5708
    c: Vertical(g18)
    c: Equal(g16,g17)
    c: Horizontal(g4,g0)
    c: Horizontal(g0,g16)
    c: Horizontal(g16,g8)
    c: Horizontal(g8,g12)
    c: Horizontal(g5,g1)
    c: Horizontal(g1,g17)
    c: Horizontal(g17,g9)
    c: Horizontal(g9,g13)
    c: DistanceX(g-1,g17) = 120
    c: Radius(g4) = 1.5
    c: Radius(g0) = 1.5
    c: Radius(g12) = 1.5
    c: Radius(g8) = 1.5
    c: Radius(g16) = 1.5
    c: DistanceX(g16,g8) = 5
    c: DistanceX(g8,g12) = 5
    c: DistanceX(g0,g16) = 5
    c: DistanceX(g4,g0) = 5
    c: DistanceY(g13,g12) = 5
    c: DistanceY(g-1,g5) = 45
FEATURE [PartDesign::Pad] Pad005
  BaseFeature = -> Pocket017
  Direction = (1,1,1)
  Length = 7
  Length2 = 100
  Profile = -> Sketch024
  Type = 0
  expr: Length = <<args>>.back_thickness - 1
FEATURE [Sketcher::SketchObject] Sketch005
  AttachmentOffset = pos=(0,0,-10) rot=(0,0,1;0rad)
  FullyConstrained = true
  MapMode = 5
  Support = -> [Pocket002]
  expr: Constraints[9] = <<args>>.button_power_offset - 2
  expr: Constraints[10] = <<args>>.pixel_h - <<args>>.screen_side_offset
  expr: .AttachmentOffset.Base.z = -<<args>>.case_thickness
  expr: Constraints[11] = <<args>>.button_volume_offset + <<args>>.button_volume_width + 2
  sketch-geometry (4):
    g0: LineSegment StartX=35 StartY=78 StartZ=0 EndX=81 EndY=78 EndZ=0
    g1: LineSegment StartX=81 StartY=78 StartZ=0 EndX=81 EndY=72.5 EndZ=0
    g2: LineSegment StartX=81 StartY=72.5 StartZ=0 EndX=35 EndY=72.5 EndZ=0
    g3: LineSegment StartX=35 StartY=72.5 StartZ=0 EndX=35 EndY=78 EndZ=0
  constraints (12):
    c: Coincident(g0,g1)
    c: Coincident(g1,g2)
    c: Coincident(g2,g3)
    c: Coincident(g3,g0)
    c: Horizontal(g0)
    c: Horizontal(g2)
    c: Vertical(g1)
    c: Vertical(g3)
    c: DistanceY(g1,g1) = 5.5
    c: DistanceX(g-1,g2) = 35
    c: DistanceY(g-1,g2) = 72.5
    c: DistanceX(g-1,g1) = 81
FEATURE [PartDesign::Pocket] Pocket003
  BaseFeature = -> Pocket002
  Length = 8
  Length2 = 100
  Profile = -> Sketch005
  Reversed = true
  Type = 0
FEATURE [PartDesign::Pocket] Pocket005  label="right-pocket"
  BaseFeature = -> Pocket003
  Length = 7
  Length2 = 100
  Profile = -> Sketch007
  Reversed = true
  Type = 0
  expr: Length = <<args>>.case_heigh_offset
FEATURE [PartDesign::Pocket] Pocket006  label="bottom-pocket"
  BaseFeature = -> Pocket005
  Length = 2
  Length2 = 100
  Profile = -> Sketch008
  Type = 0
  expr: Length = <<args>>.case_width_offset
FEATURE [PartDesign::Pocket] Pocket007  label="left-pocket"
  BaseFeature = -> Pocket006
  Length = 7
  Length2 = 100
  Profile = -> Sketch009
  Type = 0
  expr: Length = <<args>>.case_heigh_offset
FEATURE [PartDesign::Pocket] Pocket008  label="top-pocket"
  BaseFeature = -> Pocket007
  Length = 7
  Length2 = 100
  Profile = -> Sketch010
  Reversed = true
  Type = 0
  expr: Length = <<args>>.case_heigh_offset
FEATURE [PartDesign::Pocket] Pocket010  label="corner-bolt"
  BaseFeature = -> Pocket008
  Length = 8
  Length2 = 100
  Profile = -> Sketch015
  Reversed = true
  Type = 0
  expr: Length = <<args>>.case_thickness - 2
FEATURE [PartDesign::Fillet] Fillet004
  Base = -> Pocket010 [Edge58,Edge163,Edge60,Edge72]
  BaseFeature = -> Pocket010
  Radius = 8.5
  SupportTransform = false
  expr: Radius = <<args>>.pixel_corner_radius
FEATURE [PartDesign::Chamfer] Chamfer003
  Angle = 45
  Base = -> Fillet004 [Edge27,Edge25,Edge33,Edge103]
  BaseFeature = -> Fillet004
  ChamferType = 0
  FlipDirection = false
  Size = 3
  Size2 = 1
  SupportTransform = false
  expr: Size = <<args>>.case_corner_radius
FEATURE [PartDesign::Chamfer] Chamfer004
  Angle = 45
  Base = -> Chamfer003 [Edge65,Edge66,Edge63,Edge64,Edge59,Edge60,Edge62,Edge61,Edge58,Edge67,Edge68,Edge70,Edge69]
  BaseFeature = -> Chamfer003
  ChamferType = 1
  FlipDirection = false
  Size = 0.5
  Size2 = 1.6
  SupportTransform = false
FEATURE [PartDesign::Fillet] Fillet005
  Base = -> Chamfer004 [Edge38,Edge31,Edge42,Edge58,Edge34,Edge40,Edge50,Edge60]
  BaseFeature = -> Chamfer004
  Radius = 2
  SupportTransform = false
FEATURE [PartDesign::Chamfer] Chamfer005
  Angle = 45
  Base = -> Fillet005 [Edge3,Edge5,Edge7,Edge9,Edge11,Edge13,Edge15,Edge16,Edge14,Edge12,Edge10,Edge8,Edge6,Edge4,Edge2,Edge1]
  BaseFeature = -> Fillet005
  ChamferType = 1
  FlipDirection = false
  Size = 1
  Size2 = 1.5
  SupportTransform = false
FEATURE [PartDesign::Fillet] Fillet006
  Base = -> Pad005 [Edge101,Edge107,Edge109,Edge102]
  BaseFeature = -> Pad005
  Radius = 8.5
  SupportTransform = false
  expr: Radius = <<args>>.pixel_corner_radius
FEATURE [PartDesign::Chamfer] Chamfer006
  Angle = 45
  Base = -> Fillet006 [Edge28,Edge36,Edge42,Edge27]
  BaseFeature = -> Fillet006
  ChamferType = 0
  FlipDirection = false
  Size = 3
  Size2 = 1
  SupportTransform = false
  expr: Size = <<args>>.case_corner_radius
FEATURE [PartDesign::Fillet] Fillet007
  Base = -> Chamfer006 [Edge28,Edge37,Edge41,Edge119,Edge90,Edge16,Edge17,Edge23]
  BaseFeature = -> Chamfer006
  Radius = 2
  SupportTransform = false
FEATURE [Part::MultiFuse] Fusion
  Shapes = -> [Cut001001,Cut001002,Cut001003,Cut001004]
FEATURE [Part::Box] Box  label="Cube"
  AttacherType = Attacher::AttachEngine3D
  Height = 10
  Length = 50
  Placement = pos=(45,0,2) rot=(0,0,1;0rad)
  Width = 6
FEATURE [Part::Box] Box001  label="Cube001"
  AttacherType = Attacher::AttachEngine3D
  Height = 10
  Length = 50
  Placement = pos=(45,70,2) rot=(0,0,1;0rad)
  Width = 6
FEATURE [Part::MultiFuse] Fusion002
  Shapes = -> [Box,Box001]
FEATURE [Part::Cut] Cut001005  label="fan-air-channel"
  Base = -> Fusion
  Placement = pos=(-10,0,-8) rot=(0,0,1;0rad)
  Tool = -> Fusion002
FEATURE [Sketcher::SketchObject] Sketch025
  FullyConstrained = true
  MapMode = 5
  Support = -> [DatumPlane006]
  expr: Constraints[0] = <<args>>.fan_offset
  expr: Constraints[2] = <<args>>.pixel_h / 2
  sketch-geometry (12):
    g0: ArcOfCircle CenterX=65 CenterY=38 CenterZ=0 NormalX=0 NormalY=0 NormalZ=1 AngleXU=0 Radius=19 StartAngle=3.84567 EndAngle=4.00832
    g1: ArcOfCircle CenterX=49 CenterY=54 CenterZ=0 NormalX=0 NormalY=0 NormalZ=1 AngleXU=0 Radius=4 StartAngle=5.89394 EndAngle=11.3848
    g2: Circle CenterX=49 CenterY=54 CenterZ=0 NormalX=0 NormalY=0 NormalZ=1 AngleXU=0 Radius=1.9
    g3: Circle CenterX=81 CenterY=54 CenterZ=0 NormalX=0 NormalY=0 NormalZ=1 AngleXU=0 Radius=1.9
    g4: ArcOfCircle CenterX=81 CenterY=54 CenterZ=0 NormalX=0 NormalY=0 NormalZ=1 AngleXU=0 Radius=4 StartAngle=4.32314 EndAngle=9.81403
    g5: Circle CenterX=49 CenterY=22 CenterZ=0 NormalX=0 NormalY=0 NormalZ=1 AngleXU=0 Radius=1.9
    g6: ArcOfCircle CenterX=49 CenterY=22 CenterZ=0 NormalX=0 NormalY=0 NormalZ=1 AngleXU=0 Radius=4 StartAngle=1.18155 EndAngle=6.67243
    g7: Circle CenterX=81 CenterY=22 CenterZ=0 NormalX=0 NormalY=0 NormalZ=1 AngleXU=0 Radius=1.9
    g8: ArcOfCircle CenterX=81 CenterY=22 CenterZ=0 NormalX=0 NormalY=0 NormalZ=1 AngleXU=0 Radius=4 StartAngle=2.75234 EndAngle=8.24323
    g9: ArcOfCircle CenterX=65 CenterY=38 CenterZ=0 NormalX=0 NormalY=0 NormalZ=1 AngleXU=0 Radius=19 StartAngle=2.27487 EndAngle=2.43752
    g10: ArcOfCircle CenterX=65 CenterY=38 CenterZ=0 NormalX=0 NormalY=0 NormalZ=1 AngleXU=0 Radius=19 StartAngle=0.704073 EndAngle=0.866723
    g11: ArcOfCircle CenterX=65 CenterY=38 CenterZ=0 NormalX=0 NormalY=0 NormalZ=1 AngleXU=0 Radius=19 StartAngle=5.41646 EndAngle=5.57911
  constraints (37):
    c: DistanceX(g-1,g0) = 65
    c: Radius(g0) = 19
    c: DistanceY(g-1,g0) = 38
    c: Coincident(g2,g1)
    c: Coincident(g4,g3)
    c: Coincident(g6,g5)
    c: Coincident(g8,g7)
    c: Radius(g2) = 1.9
    c: Radius(g5) = 1.9
    c: Radius(g3) = 1.9
    c: Radius(g7) = 1.9
    c: Horizontal(g1,g3)
    c: Horizontal(g5,g7)
    c: Vertical(g5,g1)
    c: Vertical(g3,g7)
    c: DistanceX(g1,g0) = 16
    c: DistanceX(g0,g3) = 16
    c: DistanceY(g5,g0) = 16
    c: DistanceY(g0,g3) = 16
    c: Radius(g1) = 4
    c: Radius(g4) = 4
    c: Radius(g8) = 4
    c: Radius(g6) = 4
    c: Equal(g0,g9)
    c: Coincident(g0,g9)
    c: Equal(g0,g10)
    c: Coincident(g0,g10)
    c: Equal(g0,g11)
    c: Coincident(g0,g11)
    c: Coincident(g8,g11)
    c: Coincident(g8,g11)
    c: Coincident(g6,g0)
    c: Coincident(g6,g0)
    c: Coincident(g1,g9)
    c: Coincident(g1,g9)
    c: Coincident(g4,g10)
    c: Coincident(g4,g10)
FEATURE [PartDesign::Pad] Pad006
  BaseFeature = -> Fillet007
  Direction = (1,1,1)
  Length = 6
  Length2 = 100
  Profile = -> Sketch025
  Type = 0
  expr: Length = <<args>>.back_thickness - 2
FEATURE [Sketcher::SketchObject] Sketch027
  FullyConstrained = true
  MapMode = 5
  Placement = pos=(0,-7,-1.6e-15) rot=(1,0,0;1.5708rad)
  Support = -> [DatumPlane004]
  expr: Constraints[6] = <<args>>.pixel_w
  expr: Constraints[10] = <<args>>.pixel_w / 2
  sketch-geometry (4):
    g0: Circle CenterX=20 CenterY=4 CenterZ=0 NormalX=0 NormalY=0 NormalZ=1 AngleXU=0 Radius=1.9
    g1: Circle CenterX=135 CenterY=4 CenterZ=0 NormalX=0 NormalY=0 NormalZ=1 AngleXU=0 Radius=1.9
    g2: Circle CenterX=77.5 CenterY=4 CenterZ=0 NormalX=0 NormalY=0 NormalZ=1 AngleXU=0 Radius=1.9
    g3: GeomPoint X=155 Y=0 Z=0
  constraints (11):
    c: Horizontal(g0,g2)
    c: DistanceY(g-1,g0) = 4
    c: Radius(g0) = 1.9
    c: Radius(g2) = 1.9
    c: Radius(g1) = 1.9
    c: PointOnObject(g3,g-1)
    c: DistanceX(g-1,g3) = 155
    c: DistanceX(g-1,g0) = 20
    c: DistanceX(g1,g3) = 20
    c: Horizontal(g1,g2)
    c: DistanceX(g-1,g2) = 77.5
FEATURE [PartDesign::Pocket] Pocket019
  BaseFeature = -> Chamfer005
  Length = 10
  Length2 = 100
  Profile = -> Sketch027
  Type = 0
FEATURE [Sketcher::SketchObject] Sketch028
  FullyConstrained = true
  MapMode = 5
  Placement = pos=(0,-7,-1.6e-15) rot=(1,0,0;1.5708rad)
  Support = -> [DatumPlane009]
  expr: Constraints[1] = <<args>>.pixel_w
  expr: Constraints[9] = <<args>>.pixel_w / 2
  sketch-geometry (4):
    g0: Circle CenterX=20 CenterY=4 CenterZ=0 NormalX=0 NormalY=0 NormalZ=1 AngleXU=0 Radius=1.9
    g1: Circle CenterX=77.5 CenterY=4 CenterZ=0 NormalX=0 NormalY=0 NormalZ=1 AngleXU=0 Radius=1.9
    g2: Circle CenterX=135 CenterY=4 CenterZ=0 NormalX=0 NormalY=0 NormalZ=1 AngleXU=0 Radius=1.9
    g3: GeomPoint X=155 Y=0 Z=0
  constraints (11):
    c: PointOnObject(g3,g-1)
    c: DistanceX(g-1,g3) = 155
    c: DistanceX(g-1,g0) = 20
    c: DistanceX(g2,g3) = 20
    c: Horizontal(g0,g1)
    c: DistanceY(g-1,g0) = 4
    c: Radius(g0) = 1.9
    c: Radius(g1) = 1.9
    c: Radius(g2) = 1.9
    c: DistanceX(g-1,g1) = 77.5
    c: Horizontal(g1,g2)
FEATURE [PartDesign::Pocket] Pocket020
  BaseFeature = -> Pad006
  Length = 10
  Length2 = 100
  Profile = -> Sketch028
  Type = 0
FEATURE [Sketcher::SketchObject] Sketch029
  FullyConstrained = true
  MapMode = 5
  Placement = pos=(0,83,1.84e-14) rot=(1,0,0;1.5708rad)
  Support = -> [DatumPlane012]
  expr: Constraints[1] = <<args>>.pixel_w
  sketch-geometry (4):
    g0: GeomPoint X=155 Y=0 Z=0
    g1: Circle CenterX=20 CenterY=4 CenterZ=0 NormalX=0 NormalY=0 NormalZ=1 AngleXU=0 Radius=1.9
    g2: Circle CenterX=135 CenterY=4 CenterZ=0 NormalX=0 NormalY=0 NormalZ=1 AngleXU=0 Radius=1.9
    g3: Circle CenterX=90 CenterY=4 CenterZ=0 NormalX=0 NormalY=0 NormalZ=1 AngleXU=0 Radius=1.9
  constraints (11):
    c: PointOnObject(g0,g-1)
    c: DistanceX(g-1,g0) = 155
    c: Horizontal(g3,g1)
    c: Horizontal(g1,g2)
    c: DistanceY(g-1,g1) = 4
    c: DistanceX(g-1,g1) = 20
    c: DistanceX(g2,g0) = 20
    c: DistanceX(g3,g2) = 45
    c: Radius(g1) = 1.9
    c: Radius(g3) = 1.9
    c: Radius(g2) = 1.9
FEATURE [PartDesign::Pocket] Pocket021
  BaseFeature = -> Pocket020
  Length = 10
  Length2 = 100
  Profile = -> Sketch029
  Reversed = true
  Type = 0
FEATURE [Part::Box] Box002  label="Cube002"
  AttacherType = Attacher::AttachEngine3D
  Height = 5.5
  Length = 12
  Placement = pos=(36,75,1.25) rot=(0,0,1;0rad)
  Width = 1
FEATURE [Part::Box] Box003  label="Cube003"
  AttacherType = Attacher::AttachEngine3D
  Height = 5.5
  Length = 9.5
  Placement = pos=(37.25,76,1.25) rot=(0,0,1;0rad)
  Width = 11
FEATURE [Part::Box] Box004  label="Cube004"
  AttacherType = Attacher::AttachEngine3D
  Height = 5.5
  Length = 8
  Placement = pos=(70.75,76,1.25) rot=(0,0,1;0rad)
  Width = 11
FEATURE [Part::Box] Box005  label="Cube005"
  AttacherType = Attacher::AttachEngine3D
  Height = 5.5
  Length = 9.25
  Placement = pos=(58,75,1.25) rot=(0,0,1;0rad)
  Width = 1
FEATURE [Part::Box] Box006  label="Cube006"
  AttacherType = Attacher::AttachEngine3D
  Height = 5.5
  Length = 8
  Placement = pos=(59.25,76,1.25) rot=(0,0,1;0rad)
  Width = 11
FEATURE [Part::Box] Box007  label="Cube007"
  AttacherType = Attacher::AttachEngine3D
  Height = 5.5
  Length = 9.25
  Placement = pos=(70.75,75,1.25) rot=(0,0,1;0rad)
  Width = 1
FEATURE [Part::Box] Box008  label="Cube008"
  AttacherType = Attacher::AttachEngine3D
  Height = 5.5
  Length = 3.5
  Placement = pos=(67.25,79,1.25) rot=(0,0,1;0rad)
  Width = 2
FEATURE [Part::FeaturePython] Tube  # WARN: FeaturePython — macro-defined, semantics opaque (R4)
  AttacherType = Attacher::AttachEngine3D
  Height = 5.5
  InnerRadius = 1
  OuterRadius = 1.75
  Placement = pos=(69,81,1.25) rot=(0,0,1;0rad)
FEATURE [Part::Box] Box009  label="Cube009"
  AttacherType = Attacher::AttachEngine3D
  Height = 5.5
  Length = 1.75
  Placement = pos=(66.25,80,1.25) rot=(0,0,1;0rad)
  Width = 1
FEATURE [Part::Cut] Cut
  Base = -> Tube
  Tool = -> Box008
FEATURE [Part::Box] Box010  label="Cube010"
  AttacherType = Attacher::AttachEngine3D
  Height = 5.5
  Length = 1.75
  Placement = pos=(70,80,1.25) rot=(0,0,1;0rad)
  Width = 1
FEATURE [Part::Box] Box011  label="Cube011"
  AttacherType = Attacher::AttachEngine3D
  Height = 5.5
  Length = 4
  Placement = pos=(60,74.5,1.25) rot=(0,0,1;0rad)
  Width = 1
FEATURE [Part::Box] Box012  label="Cube012"
  AttacherType = Attacher::AttachEngine3D
  Height = 5.5
  Length = 4
  Placement = pos=(74,74.5,1.25) rot=(0,0,1;0rad)
  Width = 1
FEATURE [Part::MultiFuse] Fusion004
  Refine = true
  Shapes = -> [Box012,Box011,Box010,Cut,Box009,Box007,Box006,Box005,Box004]
FEATURE [Part::Box] Box013  label="Cube013"
  AttacherType = Attacher::AttachEngine3D
  Height = 5.5
  Length = 8
  Placement = pos=(38,74.5,1.25) rot=(0,0,1;0rad)
  Width = 1
FEATURE [Part::MultiFuse] Fusion005
  Refine = true
  Shapes = -> [Box013,Box002,Box003]
FEATURE [Part::Chamfer] Chamfer011
  Base = -> Fusion005
  Edges = 2 edges r=0.4: [Edge4,Edge9]
FEATURE [Part::Chamfer] Chamfer012
  Base = -> Fusion004
  Edges = 6 edges r=0.4: [Edge7,Edge10,Edge21,Edge26,Edge74,Edge79]
FEATURE [Part::Chamfer] Chamfer013
  Base = -> Chamfer012
  Edges = 2 edges r=2: [Edge41,Edge76]
FEATURE [Part::Chamfer] Chamfer014  label="power-btn"
  Base = -> Chamfer011
  Edges = 2 edges r=1: [Edge38,Edge40]
  Placement = pos=(0,2,0) rot=(0,0,1;0rad)
FEATURE [Part::Chamfer] Chamfer015  label="volume-btn"
  Base = -> Chamfer013
  Edges = 4 edges r=1: [Edge74,Edge79,Edge90,Edge95]
  Placement = pos=(0,2,0) rot=(0,0,1;0rad)
FEATURE [Sketcher::SketchObject] Sketch032
  FullyConstrained = true
  MapMode = 5
  Support = -> [XY_Plane002]
  expr: Constraints[20] = <<args>>.case_heigh_offset + 0.15
  expr: Constraints[21] = <<args>>.case_width_offset + 0.15
  expr: Constraints[22] = <<args>>.case_width_offset * 2 + <<args>>.pixel_w + 0.3
  sketch-geometry (8):
    g0: LineSegment StartX=-5.15 StartY=12 StartZ=0 EndX=-2.15 EndY=12 EndZ=0
    g1: LineSegment StartX=-2.15 StartY=12 StartZ=0 EndX=-2.15 EndY=-7.15 EndZ=0
    g2: LineSegment StartX=-2.15 StartY=-7.15 StartZ=0 EndX=157.15 EndY=-7.15 EndZ=0
    g3: LineSegment StartX=157.15 StartY=-7.15 StartZ=0 EndX=157.15 EndY=12 EndZ=0
    g4: LineSegment StartX=157.15 StartY=12 StartZ=0 EndX=160.15 EndY=12 EndZ=0
    g5: LineSegment StartX=160.15 StartY=12 StartZ=0 EndX=160.15 EndY=-10.15 EndZ=0
    g6: LineSegment StartX=160.15 StartY=-10.15 StartZ=0 EndX=-5.15 EndY=-10.15 EndZ=0
    g7: LineSegment StartX=-5.15 StartY=-10.15 StartZ=0 EndX=-5.15 EndY=12 EndZ=0
  constraints (24):
    c: Horizontal(g0)
    c: Coincident(g0,g1)
    c: Vertical(g1)
    c: Coincident(g1,g2)
    c: Horizontal(g2)
    c: Coincident(g2,g3)
    c: Vertical(g3)
    c: Coincident(g3,g4)
    c: Horizontal(g4)
    c: Coincident(g4,g5)
    c: Vertical(g5)
    c: Coincident(g5,g6)
    c: Horizontal(g6)
    c: Coincident(g6,g7)
    c: Coincident(g7,g0)
    c: Vertical(g7)
    c: DistanceX(g0,g0) = 3
    c: DistanceX(g4,g4) = 3
    c: DistanceY(g6,g1) = 3
    c: DistanceY(g-1,g0) = 12
    c: DistanceY(g1,g-1) = 7.15
    c: DistanceX(g0,g-1) = 2.15
    c: DistanceX(g2,g2) = 159.3
    c: DistanceY(g-1,g3) = 12
FEATURE [PartDesign::Pad] Pad007
  Direction = (1,1,1)
  Length = 16
  Length2 = 100
  Profile = -> Sketch032
  Type = 0
FEATURE [PartDesign::Chamfer] Chamfer016
  Angle = 45
  Base = -> Pad007 [Edge8,Edge5]
  BaseFeature = -> Pad007
  ChamferType = 0
  FlipDirection = false
  Size = 3
  Size2 = 1
  SupportTransform = false
FEATURE [PartDesign::Fillet] Fillet
  Base = -> Chamfer016 [Edge2,Edge14,Edge25,Edge27]
  BaseFeature = -> Chamfer016
  Radius = 2
  SupportTransform = false
FEATURE [PartDesign::Chamfer] Chamfer017
  Angle = 45
  Base = -> Fillet [Edge34,Edge36]
  BaseFeature = -> Fillet
  ChamferType = 0
  FlipDirection = false
  Size = 3.5
  Size2 = 1
  SupportTransform = false
FEATURE [PartDesign::Fillet] Fillet008
  Base = -> Chamfer017 [Edge17,Edge20,Edge24,Edge28]
  BaseFeature = -> Chamfer017
  Radius = 2
  SupportTransform = false
FEATURE [Sketcher::SketchObject] Sketch040
  FullyConstrained = true
  MapMode = 5
  Support = -> [DatumPlane006]
  expr: Constraints[8] = <<args>>.wiring_hole_offset - 20
  expr: Constraints[9] = <<args>>.pixel_h - 9
  sketch-geometry (4):
    g0: ArcOfCircle CenterX=90 CenterY=67 CenterZ=0 NormalX=0 NormalY=0 NormalZ=1 AngleXU=0 Radius=1.5 StartAngle=1.5708 EndAngle=4.71239
    g1: ArcOfCircle CenterX=100 CenterY=67 CenterZ=0 NormalX=0 NormalY=0 NormalZ=1 AngleXU=0 Radius=1.5 StartAngle=4.71239 EndAngle=7.85398
    g2: LineSegment StartX=90 StartY=65.5 StartZ=0 EndX=100 EndY=65.5 EndZ=0
    g3: LineSegment StartX=90 StartY=68.5 StartZ=0 EndX=100 EndY=68.5 EndZ=0
  constraints (10):
    c: Tangent(g0,g3) = 1.5708
    c: Tangent(g0,g2) = -1.5708
    c: Tangent(g2,g1) = -1.5708
    c: Tangent(g3,g1) = 1.5708
    c: Horizontal(g2)
    c: Equal(g0,g1)
    c: DistanceX(g0,g1) = 10
    c: Radius(g0) = 1.5
    c: DistanceX(g-1,g1) = 100
    c: DistanceY(g-1,g1) = 67
FEATURE [PartDesign::Pad] Pad009
  BaseFeature = -> Pocket021
  Direction = (1,1,1)
  Length = 7
  Length2 = 100
  Profile = -> Sketch040
  Type = 0
  expr: Length = <<args>>.back_thickness - 1
FEATURE [Sketcher::SketchObject] Sketch041
  FullyConstrained = true
  MapMode = 5
  Support = -> [DatumPlane006]
  expr: Constraints[11] = <<args>>.case_width_offset
  expr: Constraints[10] = <<args>>.case_width_offset
  expr: Constraints[9] = <<args>>.headphone_jack_center_offset - <<args>>.headphone_jack_width / 2
  expr: Constraints[8] = <<args>>.headphone_jack_width
  sketch-geometry (4):
    g0: LineSegment StartX=-2 StartY=26 StartZ=0 EndX=-2e-16 EndY=26 EndZ=0
    g1: LineSegment StartX=-2e-16 StartY=26 StartZ=0 EndX=-2e-16 EndY=18 EndZ=0
    g2: LineSegment StartX=-2e-16 StartY=18 StartZ=0 EndX=-2 EndY=18 EndZ=0
    g3: LineSegment StartX=-2 StartY=18 StartZ=0 EndX=-2 EndY=26 EndZ=0
  constraints (12):
    c: Coincident(g0,g1)
    c: Coincident(g1,g2)
    c: Coincident(g2,g3)
    c: Coincident(g3,g0)
    c: Horizontal(g0)
    c: Horizontal(g2)
    c: Vertical(g1)
    c: Vertical(g3)
    c: DistanceY(g3,g3) = 8
    c: DistanceY(g-1,g2) = 18
    c: DistanceX(g2,g-1) = 2
    c: DistanceX(g2,g2) = 2
FEATURE [PartDesign::Pocket] Pocket030
  BaseFeature = -> Pad009
  Length = 5
  Length2 = 100
  Profile = -> Sketch041
  Reversed = true
  Type = 1
FEATURE [Sketcher::SketchObject] Sketch035
  FullyConstrained = true
  MapMode = 5
  Support = -> [XY_Plane003]
  expr: Constraints[18] = <<args>>.case_width_offset * 2 + <<args>>.pixel_w + 0.3
  expr: Constraints[19] = <<args>>.case_width_offset + 0.15
  expr: Constraints[20] = <<args>>.pixel_h / 2 - 11
  expr: Constraints[21] = <<args>>.case_heigh_offset + <<args>>.pixel_h / 2 + 0.15 + 11
  sketch-geometry (8):
    g0: LineSegment StartX=-5.15 StartY=27 StartZ=0 EndX=-2.15 EndY=27 EndZ=0
    g1: LineSegment StartX=-2.15 StartY=27 StartZ=0 EndX=-2.15 EndY=83.15 EndZ=0
    g2: LineSegment StartX=-2.15 StartY=83.15 StartZ=0 EndX=157.15 EndY=83.15 EndZ=0
    g3: LineSegment StartX=157.15 StartY=83.15 StartZ=0 EndX=157.15 EndY=27 EndZ=0
    g4: LineSegment StartX=157.15 StartY=27 StartZ=0 EndX=160.15 EndY=27 EndZ=0
    g5: LineSegment StartX=160.15 StartY=27 StartZ=0 EndX=160.15 EndY=86.15 EndZ=0
    g6: LineSegment StartX=160.15 StartY=86.15 StartZ=0 EndX=-5.15 EndY=86.15 EndZ=0
    g7: LineSegment StartX=-5.15 StartY=86.15 StartZ=0 EndX=-5.15 EndY=27 EndZ=0
  constraints (24):
    c: Coincident(g0,g1)
    c: Vertical(g1)
    c: Coincident(g1,g2)
    c: Horizontal(g2)
    c: Coincident(g2,g3)
    c: Vertical(g3)
    c: Coincident(g3,g4)
    c: Horizontal(g4)
    c: Coincident(g4,g5)
    c: Vertical(g5)
    c: Coincident(g5,g6)
    c: Horizontal(g6)
    c: Coincident(g6,g7)
    c: Coincident(g7,g0)
    c: Vertical(g7)
    c: Horizontal(g0)
    c: DistanceX(g0,g0) = 3
    c: DistanceX(g4,g4) = 3
    c: DistanceX(g2,g2) = 159.3
    c: DistanceX(g0,g-1) = 2.15
    c: DistanceY(g-1,g0) = 27
    c: DistanceY(g1,g1) = 56.15
    c: DistanceY(g1,g6) = 3
    c: Horizontal(g3,g0)
FEATURE [PartDesign::Pad] Pad008
  Direction = (1,1,1)
  Length = 33
  Length2 = 100
  Profile = -> Sketch035
  Type = 0
  expr: Length = <<args>>.case_thickness + <<args>>.back_thickness + <<args>>.sun_visor_heigh
FEATURE [PartDesign::Chamfer] Chamfer021
  Angle = 45
  Base = -> Pad008 [Edge5,Edge8]
  BaseFeature = -> Pad008
  ChamferType = 0
  FlipDirection = false
  Size = 3
  Size2 = 1
  SupportTransform = false
FEATURE [PartDesign::Fillet] Fillet009
  Base = -> Chamfer021 [Edge2,Edge14,Edge25,Edge27]
  BaseFeature = -> Chamfer021
  Radius = 2
  SupportTransform = false
FEATURE [PartDesign::Chamfer] Chamfer022
  Angle = 45
  Base = -> Fillet009 [Edge34,Edge36]
  BaseFeature = -> Fillet009
  ChamferType = 0
  FlipDirection = false
  Size = 3.5
  Size2 = 1
  SupportTransform = false
FEATURE [Sketcher::SketchObject] Sketch036
  FullyConstrained = true
  MapMode = 5
  Placement = pos=(0,86.15,0) rot=(0,0.707107,0.707107;3.14159rad)
  Support = -> [Chamfer022]
  expr: Constraints[8] = <<args>>.back_thickness + 1
  expr: Constraints[9] = <<args>>.pixel_t - 2 + 0.2
  expr: Constraints[22] = <<args>>.back_thickness + 1
  expr: Constraints[10] = <<args>>.button_power_offset
  expr: Constraints[11] = <<args>>.button_power_width
  expr: Constraints[13] = <<args>>.pixel_w
  expr: Constraints[23] = <<args>>.pixel_t - 2 + 0.2
  expr: Constraints[24] = <<args>>.button_volume_offset
  expr: Constraints[25] = <<args>>.button_volume_width
  sketch-geometry (15):
    g0: LineSegment StartX=-47 StartY=15.2 StartZ=0 EndX=-37 EndY=15.2 EndZ=0
    g1: LineSegment StartX=-37 StartY=15.2 StartZ=0 EndX=-37 EndY=9 EndZ=0
    g2: LineSegment StartX=-37 StartY=9 StartZ=0 EndX=-47 EndY=9 EndZ=0
    g3: LineSegment StartX=-47 StartY=9 StartZ=0 EndX=-47 EndY=15.2 EndZ=0
    g4: GeomPoint X=-155 Y=0 Z=0
    g5: LineSegment StartX=-79 StartY=15.2 StartZ=0 EndX=-59 EndY=15.2 EndZ=0
    g6: LineSegment StartX=-59 StartY=15.2 StartZ=0 EndX=-59 EndY=9 EndZ=0
    g7: LineSegment StartX=-59 StartY=9 StartZ=0 EndX=-79 EndY=9 EndZ=0
    g8: LineSegment StartX=-79 StartY=9 StartZ=0 EndX=-79 EndY=15.2 EndZ=0
    g9: Circle CenterX=-135 CenterY=12 CenterZ=0 NormalX=0 NormalY=0 NormalZ=1 AngleXU=0 Radius=1.65
    g10: Circle CenterX=-135 CenterY=4 CenterZ=0 NormalX=0 NormalY=0 NormalZ=1 AngleXU=0 Radius=1.65
    g11: Circle CenterX=-90 CenterY=12 CenterZ=0 NormalX=0 NormalY=0 NormalZ=1 AngleXU=0 Radius=1.65
    g12: Circle CenterX=-90 CenterY=4 CenterZ=0 NormalX=0 NormalY=0 NormalZ=1 AngleXU=0 Radius=1.65
    g13: Circle CenterX=-20 CenterY=12 CenterZ=0 NormalX=0 NormalY=0 NormalZ=1 AngleXU=0 Radius=1.65
    g14: Circle CenterX=-20 CenterY=4 CenterZ=0 NormalX=0 NormalY=0 NormalZ=1 AngleXU=0 Radius=1.65
  constraints (44):
    c: Coincident(g0,g1)
    c: Coincident(g1,g2)
    c: Coincident(g2,g3)
    c: Coincident(g3,g0)
    c: Horizontal(g0)
    c: Horizontal(g2)
    c: Vertical(g1)
    c: Vertical(g3)
    c: DistanceY(g-1,g1) = 9
    c: DistanceY(g1,g1) = 6.2
    c: DistanceX(g1,g-1) = 37
    c: DistanceX(g2,g2) = 10
    c: PointOnObject(g4,g-1)
    c: DistanceX(g4,g-1) = 155
    c: Coincident(g5,g6)
    c: Coincident(g6,g7)
    c: Coincident(g7,g8)
    c: Coincident(g8,g5)
    c: Horizontal(g5)
    c: Horizontal(g7)
    c: Vertical(g6)
    c: Vertical(g8)
    c: DistanceY(g-1,g6) = 9
    c: DistanceY(g6,g6) = 6.2
    c: DistanceX(g6,g-1) = 59
    c: DistanceX(g5,g5) = 20
    c: Radius(g9) = 1.65
    c: Radius(g10) = 1.65
    c: Radius(g11) = 1.65
    c: Radius(g12) = 1.65
    c: Radius(g13) = 1.65
    c: Radius(g14) = 1.65
    c: Vertical(g9,g10)
    c: Vertical(g11,g12)
    c: Vertical(g13,g14)
    c: Horizontal(g9,g11)
    c: Horizontal(g11,g13)
    c: Horizontal(g10,g12)
    c: Horizontal(g12,g14)
    c: DistanceX(g14,g-1) = 20
    c: DistanceY(g-1,g14) = 4
    c: DistanceY(g14,g13) = 8
    c: DistanceX(g4,g10) = 20
    c: DistanceX(g10,g12) = 45
FEATURE [PartDesign::Pocket] Pocket026
  BaseFeature = -> Chamfer022
  Length = 5
  Length2 = 100
  Profile = -> Sketch036
  Type = 1
FEATURE [Sketcher::SketchObject] Sketch037
  FullyConstrained = true
  MapMode = 5
  Placement = pos=(160.15,0,0) rot=(0.57735,0.57735,0.57735;2.0944rad)
  Support = -> [Pocket026]
  sketch-geometry (2):
    g0: Circle CenterX=33 CenterY=4 CenterZ=0 NormalX=0 NormalY=0 NormalZ=1 AngleXU=0 Radius=1.65
    g1: Circle CenterX=68 CenterY=4 CenterZ=0 NormalX=0 NormalY=0 NormalZ=1 AngleXU=0 Radius=1.65
  constraints (6):
    c: Radius(g0) = 1.65
    c: DistanceY(g-1,g0) = 4
    c: DistanceX(g-1,g0) = 33
    c: Radius(g1) = 1.65
    c: Horizontal(g1,g0)
    c: DistanceX(g0,g1) = 35
FEATURE [PartDesign::Pocket] Pocket027
  BaseFeature = -> Pocket026
  Length = 5
  Length2 = 100
  Profile = -> Sketch037
  Type = 1
FEATURE [Sketcher::SketchObject] Sketch038
  FullyConstrained = true
  MapMode = 5
  Placement = pos=(160.15,0,0) rot=(0.57735,0.57735,0.57735;2.0944rad)
  Support = -> [Pocket027]
  expr: Constraints[5] = <<args>>.case_thickness + <<args>>.back_thickness + <<args>>.sun_visor_heigh
  expr: Constraints[4] = <<args>>.sun_visor_ramp_width
  sketch-geometry (3):
    g0: LineSegment StartX=27 StartY=10 StartZ=0 EndX=67 EndY=33 EndZ=0
    g1: LineSegment StartX=27 StartY=33 StartZ=0 EndX=27 EndY=10 EndZ=0
    g2: LineSegment StartX=27 StartY=33 StartZ=0 EndX=67 EndY=33 EndZ=0
  constraints (9):
    c: Coincident(g1,g0)
    c: Vertical(g1)
    c: DistanceX(g-1,g0) = 27
    c: DistanceY(g-1,g0) = 10
    c: DistanceX(g0,g0) = 40
    c: DistanceY(g-1,g1) = 33
    c: Coincident(g2,g1)
    c: Coincident(g2,g0)
    c: Horizontal(g2)
FEATURE [PartDesign::Pocket] Pocket028
  BaseFeature = -> Pocket027
  Length = 5
  Length2 = 100
  Profile = -> Sketch038
  Type = 1
FEATURE [Sketcher::SketchObject] Sketch039
  FullyConstrained = true
  MapMode = 5
  Placement = pos=(160.15,0,0) rot=(0.57735,0.57735,0.57735;2.0944rad)
  Support = -> [Pocket028]
  expr: Constraints[11] = <<args>>.back_thickness + 1
  expr: Constraints[10] = <<args>>.pixel_t - 2 + 0.2
  expr: Constraints[9] = <<args>>.pixel_h - <<args>>.spekaer_offset + 2
  expr: Constraints[8] = <<args>>.speaker_width + 4
  sketch-geometry (4):
    g0: LineSegment StartX=49 StartY=15.2 StartZ=0 EndX=64 EndY=15.2 EndZ=0
    g1: LineSegment StartX=64 StartY=15.2 StartZ=0 EndX=64 EndY=9 EndZ=0
    g2: LineSegment StartX=64 StartY=9 StartZ=0 EndX=49 EndY=9 EndZ=0
    g3: LineSegment StartX=49 StartY=9 StartZ=0 EndX=49 EndY=15.2 EndZ=0
  constraints (12):
    c: Coincident(g0,g1)
    c: Coincident(g1,g2)
    c: Coincident(g2,g3)
    c: Coincident(g3,g0)
    c: Horizontal(g0)
    c: Horizontal(g2)
    c: Vertical(g1)
    c: Vertical(g3)
    c: DistanceX(g0,g0) = 15
    c: DistanceX(g-1,g1) = 64
    c: DistanceY(g3,g3) = 6.2
    c: DistanceY(g-1,g2) = 9
FEATURE [PartDesign::Pocket] Pocket029
  BaseFeature = -> Pocket028
  Length = 2
  Length2 = 100
  Profile = -> Sketch039
  Type = 0
FEATURE [Sketcher::SketchObject] Sketch042
  FullyConstrained = true
  MapMode = 5
  Placement = pos=(160.15,0,0) rot=(0.57735,0.57735,0.57735;2.0944rad)
  Support = -> [Fillet008]
  sketch-geometry (4):
    g0: LineSegment StartX=-2 StartY=16 StartZ=0 EndX=12 EndY=16 EndZ=0
    g1: LineSegment StartX=12 StartY=16 StartZ=0 EndX=12 EndY=10 EndZ=0
    g2: LineSegment StartX=12 StartY=10 StartZ=0 EndX=-2 EndY=16 EndZ=0
    g3: Circle CenterX=7 CenterY=4 CenterZ=0 NormalX=0 NormalY=0 NormalZ=1 AngleXU=0 Radius=1.65
  constraints (12):
    c: Horizontal(g0)
    c: Coincident(g0,g1)
    c: Vertical(g1)
    c: Coincident(g1,g2)
    c: Coincident(g2,g0)
    c: DistanceX(g-1,g0) = -2
    c: DistanceX(g-1,g1) = 12
    c: DistanceY(g-1,g1) = 10
    c: DistanceY(g-1,g0) = 16
    c: Radius(g3) = 1.65
    c: DistanceX(g-1,g3) = 7
    c: DistanceY(g-1,g3) = 4
FEATURE [PartDesign::Pocket] Pocket031
  BaseFeature = -> Fillet008
  Length = 5
  Length2 = 100
  Profile = -> Sketch042
  Type = 1
FEATURE [Sketcher::SketchObject] Sketch043
  FullyConstrained = true
  MapMode = 5
  Placement = pos=(0,-10.15,0) rot=(1,0,0;1.5708rad)
  Support = -> [Pocket031]
  expr: Constraints[19] = <<args>>.pixel_w / 2
  expr: Constraints[14] = <<args>>.pixel_w
  sketch-geometry (7):
    g0: Circle CenterX=20 CenterY=4 CenterZ=0 NormalX=0 NormalY=0 NormalZ=1 AngleXU=0 Radius=1.65
    g1: Circle CenterX=20 CenterY=12 CenterZ=0 NormalX=0 NormalY=0 NormalZ=1 AngleXU=0 Radius=1.65
    g2: Circle CenterX=77.5 CenterY=12 CenterZ=0 NormalX=0 NormalY=0 NormalZ=1 AngleXU=0 Radius=1.65
    g3: Circle CenterX=135 CenterY=12 CenterZ=0 NormalX=0 NormalY=0 NormalZ=1 AngleXU=0 Radius=1.65
    g4: Circle CenterX=135 CenterY=4 CenterZ=0 NormalX=0 NormalY=0 NormalZ=1 AngleXU=0 Radius=1.65
    g5: Circle CenterX=77.5 CenterY=4 CenterZ=0 NormalX=0 NormalY=0 NormalZ=1 AngleXU=0 Radius=1.65
    g6: GeomPoint X=155 Y=0 Z=0
  constraints (20):
    c: Horizontal(g1,g2)
    c: Horizontal(g2,g3)
    c: Horizontal(g0,g5)
    c: Horizontal(g5,g4)
    c: Vertical(g1,g0)
    c: Vertical(g2,g5)
    c: Vertical(g3,g4)
    c: Radius(g1) = 1.65
    c: Radius(g0) = 1.65
    c: Radius(g2) = 1.65
    c: Radius(g5) = 1.65
    c: Radius(g3) = 1.65
    c: Radius(g4) = 1.65
    c: PointOnObject(g6,g-1)
    c: DistanceX(g-1,g6) = 155
    c: DistanceX(g-1,g0) = 20
    c: DistanceX(g4,g6) = 20
    c: DistanceY(g-1,g0) = 4
    c: DistanceY(g-1,g1) = 12
    c: DistanceX(g-1,g5) = 77.5
FEATURE [PartDesign::Pocket] Pocket032
  BaseFeature = -> Pocket031
  Length = 5
  Length2 = 100
  Profile = -> Sketch043
  Type = 1
FEATURE [Sketcher::SketchObject] Sketch044
  FullyConstrained = true
  MapMode = 5
  Placement = pos=(157,-3.49e-14,3.49e-14) rot=(0.57735,0.57735,0.57735;2.0944rad)
  Support = -> [DatumPlane011]
  sketch-geometry (3):
    g0: Circle CenterX=7 CenterY=4 CenterZ=0 NormalX=0 NormalY=0 NormalZ=1 AngleXU=0 Radius=1.9
    g1: Circle CenterX=33 CenterY=4 CenterZ=0 NormalX=0 NormalY=0 NormalZ=1 AngleXU=0 Radius=1.9
    g2: Circle CenterX=68 CenterY=4 CenterZ=0 NormalX=0 NormalY=0 NormalZ=1 AngleXU=0 Radius=1.9
  constraints (9):
    c: Radius(g0) = 1.9
    c: DistanceY(g-1,g0) = 4
    c: Horizontal(g2,g1)
    c: Horizontal(g1,g0)
    c: Radius(g1) = 1.9
    c: Radius(g2) = 1.9
    c: DistanceX(g-1,g0) = 7
    c: DistanceX(g-1,g1) = 33
    c: DistanceX(g-1,g2) = 68
FEATURE [PartDesign::Pocket] Pocket033
  BaseFeature = -> Pocket030
  Length = 7
  Length2 = 100
  Profile = -> Sketch044
  Type = 0
FEATURE [Sketcher::SketchObject] Sketch045
  FullyConstrained = true
  MapMode = 5
  Placement = pos=(-2,4e-16,-4e-16) rot=(0.57735,0.57735,0.57735;2.0944rad)
  Support = -> [DatumPlane010]
  sketch-geometry (3):
    g0: Circle CenterX=7 CenterY=4 CenterZ=0 NormalX=0 NormalY=0 NormalZ=1 AngleXU=0 Radius=1.9
    g1: Circle CenterX=33 CenterY=4 CenterZ=0 NormalX=0 NormalY=0 NormalZ=1 AngleXU=0 Radius=1.9
    g2: Circle CenterX=68 CenterY=4 CenterZ=0 NormalX=0 NormalY=0 NormalZ=1 AngleXU=0 Radius=1.9
  constraints (9):
    c: DistanceX(g-1,g0) = 7
    c: DistanceX(g-1,g1) = 33
    c: DistanceX(g-1,g2) = 68
    c: Horizontal(g0,g1)
    c: Horizontal(g1,g2)
    c: DistanceY(g-1,g0) = 4
    c: Radius(g0) = 1.9
    c: Radius(g1) = 1.9
    c: Radius(g2) = 1.9
FEATURE [PartDesign::Pocket] Pocket034
  BaseFeature = -> Pocket033
  Length = 7
  Length2 = 100
  Profile = -> Sketch045
  Reversed = true
  Type = 0
FEATURE [PartDesign::Fillet] Fillet010
  Base = -> Pocket029 [Edge48,Edge27,Edge23,Edge20]
  BaseFeature = -> Pocket029
  Radius = 2
  SupportTransform = false
FEATURE [PartDesign::Chamfer] Chamfer
  Angle = 45
  Base = -> Fillet010 [Edge3,Edge18]
  BaseFeature = -> Fillet010
  ChamferType = 0
  FlipDirection = false
  Size = 1
  Size2 = 1
  SupportTransform = false
FEATURE [PartDesign::Fillet] Fillet011
  Base = -> Chamfer [Edge132,Edge115,Edge114,Edge113]
  BaseFeature = -> Chamfer
  Radius = 3
  SupportTransform = false
FEATURE [PartDesign::Chamfer] Chamfer023
  Angle = 45
  Base = -> Pocket032 [Edge3,Edge18]
  BaseFeature = -> Pocket032
  ChamferType = 0
  FlipDirection = false
  Size = 1
  Size2 = 1
  SupportTransform = false
FEATURE [PartDesign::Fillet] Fillet012
  Base = -> Chamfer023 [Edge87,Edge85,Edge95,Edge86]
  BaseFeature = -> Chamfer023
  Radius = 2
  SupportTransform = false
FEATURE [PartDesign::Chamfer] Chamfer024
  Angle = 45
  Base = -> Fillet011 [Edge4,Edge6,Edge8,Edge41,Edge43,Edge45,Edge47,Edge38,Edge18,Edge42,Edge44,Edge46,Edge48,Edge50,Edge49,Edge51,Edge53,Edge55,Edge52,Edge54,Edge56,Edge58,Edge121,Edge108,Edge107,Edge120,Edge119,Edge105,Edge104,Edge118,Edge116,Edge106,Edge34,Edge37,Edge28,Edge30,Edge32,Edge35,Edge33,Edge31,+38 more]
  BaseFeature = -> Fillet011
  ChamferType = 0
  FlipDirection = false
  Size = 0.4
  Size2 = 1
  SupportTransform = false
FEATURE [PartDesign::Body] Body004015  label="top-cover"
  Group = -> [Sketch035,Pad008,Chamfer021,Fillet009,Chamfer022,Sketch036,Pocket026,Sketch037,Pocket027,Sketch038,Pocket028,Sketch039,Pocket029,Fillet010,Chamfer,Fillet011,Chamfer024]
  Origin = -> Origin003
  Placement = pos=(0,0,-8) rot=(0,0,1;0rad)
  Tip = -> Chamfer024
  expr: .Placement.Base.z = -<<args>>.back_thickness
FEATURE [PartDesign::Chamfer] Chamfer025
  Angle = 45
  Base = -> Fillet012 [Edge9,Edge3,Edge16,Edge1,Edge10,Edge13,Edge2,Edge4,Edge17,Edge37,Edge6,Edge8,Edge40,Edge56,Edge57,Edge55,Edge54,Edge52,Edge53,Edge51,Edge49,Edge44,Edge96,Edge97,Edge46,Edge48,Edge50,Edge47,Edge45,Edge43,Edge41,Edge89,Edge88,Edge86,Edge95,Edge94,Edge85,Edge87,Edge92,Edge33,+24 more]
  BaseFeature = -> Fillet012
  ChamferType = 0
  FlipDirection = false
  Size = 0.4
  Size2 = 1
  SupportTransform = false
FEATURE [PartDesign::Body] Body004014  label="bottom-cover"
  Group = -> [Sketch032,Pad007,Chamfer016,Fillet,Chamfer017,Fillet008,Sketch042,Pocket031,Sketch043,Pocket032,Chamfer023,Fillet012,Chamfer025]
  Origin = -> Origin002
  Placement = pos=(0,0,-8) rot=(0,0,1;0rad)
  Tip = -> Chamfer025
  expr: .Placement.Base.z = -<<args>>.back_thickness
FEATURE [PartDesign::Chamfer] Chamfer026
  Angle = 45
  Base = -> Pocket034 [Edge57,Edge56,Edge12,Edge47,Edge45,Edge43,Edge39,Edge36,Edge55,Edge54,Edge53,Edge52,Edge51,Edge50,Edge63,Edge62,Edge61,Edge60,Edge59,Edge65,Edge100,Edge48,Edge64]
  BaseFeature = -> Pocket034
  ChamferType = 0
  FlipDirection = false
  Size = 0.4
  Size2 = 1
  SupportTransform = false
FEATURE [PartDesign::Chamfer] Chamfer027
  Angle = 45
  Base = -> Chamfer026 [Edge163,Edge162,Edge275,Edge285,Edge286,Edge287,Edge122,Edge123,Edge124,Edge9,Edge10,Edge11]
  BaseFeature = -> Chamfer026
  ChamferType = 0
  FlipDirection = false
  Size = 0.4
  Size2 = 1
  SupportTransform = false
FEATURE [Sketcher::SketchObject] Sketch046
  FullyConstrained = true
  MapMode = 5
  Placement = pos=(0,83,1.84e-14) rot=(1,0,0;1.5708rad)
  Support = -> [DatumPlane002]
  expr: Constraints[4] = <<args>>.pixel_w
  sketch-geometry (4):
    g0: Circle CenterX=20 CenterY=4 CenterZ=0 NormalX=0 NormalY=0 NormalZ=1 AngleXU=0 Radius=1.9
    g1: Circle CenterX=90 CenterY=4 CenterZ=0 NormalX=0 NormalY=0 NormalZ=1 AngleXU=0 Radius=1.9
    g2: Circle CenterX=135 CenterY=4 CenterZ=0 NormalX=0 NormalY=0 NormalZ=1 AngleXU=0 Radius=1.9
    g3: GeomPoint X=155 Y=0 Z=0
  constraints (11):
    c: Horizontal(g2,g1)
    c: Horizontal(g1,g0)
    c: DistanceY(g-1,g0) = 4
    c: PointOnObject(g3,g-1)
    c: DistanceX(g-1,g3) = 155
    c: Radius(g0) = 1.9
    c: Radius(g1) = 1.9
    c: Radius(g2) = 1.9
    c: DistanceX(g2,g3) = 20
    c: DistanceX(g-1,g0) = 20
    c: DistanceX(g-1,g1) = 90
FEATURE [PartDesign::Pocket] Pocket035
  BaseFeature = -> Pocket019
  Length = 10
  Length2 = 100
  Profile = -> Sketch046
  Reversed = true
  Type = 0
FEATURE [PartDesign::Chamfer] Chamfer028
  Angle = 45
  Base = -> Pocket035 [Edge146,Edge147,Edge148,Edge97,Edge98,Edge99]
  BaseFeature = -> Pocket035
  ChamferType = 0
  FlipDirection = false
  Size = 0.4
  Size2 = 1
  SupportTransform = false
FEATURE [PartDesign::Body] Body  label="front"
  Group = -> [Sketch,Pad,DatumPlane,Sketch001,Pocket,DatumPlane001,Sketch002,Pocket001,Sketch003,Pocket002,Sketch005,Pocket003,DatumPlane002,Sketch007,Pocket005,DatumPlane003,Sketch008,Pocket006,DatumPlane004,Sketch009,Pocket007,DatumPlane005,Sketch010,Pocket008,Sketch015,Pocket010,Fillet004,Chamfer003,Chamfer004,Fillet005,Chamfer005,Sketch027,Pocket019,Sketch046,Pocket035,Chamfer028]
  Origin = -> Origin
  Tip = -> Chamfer028
FEATURE [Sketcher::SketchObject] Sketch047
  FullyConstrained = true
  MapMode = 5
  Support = -> [DatumPlane006]
  expr: Constraints[9] = (<<args>>.pixel_h - 65) / 2
  expr: Constraints[16] = <<args>>.pixel_w
  sketch-geometry (9):
    g0: Circle CenterX=9 CenterY=70.5 CenterZ=0 NormalX=0 NormalY=0 NormalZ=1 AngleXU=0 Radius=1.9
    g1: Circle CenterX=9 CenterY=5.5 CenterZ=0 NormalX=0 NormalY=0 NormalZ=1 AngleXU=0 Radius=1.9
    g2: Circle CenterX=146 CenterY=5.5 CenterZ=0 NormalX=0 NormalY=0 NormalZ=1 AngleXU=0 Radius=1.9
    g3: Circle CenterX=146 CenterY=70.5 CenterZ=0 NormalX=0 NormalY=0 NormalZ=1 AngleXU=0 Radius=1.9
    g4: Circle CenterX=21 CenterY=60.5 CenterZ=0 NormalX=0 NormalY=0 NormalZ=1 AngleXU=0 Radius=1.9
    g5: Circle CenterX=21 CenterY=15.5 CenterZ=0 NormalX=0 NormalY=0 NormalZ=1 AngleXU=0 Radius=1.9
    g6: Circle CenterX=134 CenterY=60.5 CenterZ=0 NormalX=0 NormalY=0 NormalZ=1 AngleXU=0 Radius=1.9
    g7: Circle CenterX=134 CenterY=15.5 CenterZ=0 NormalX=0 NormalY=0 NormalZ=1 AngleXU=0 Radius=1.9
    g8: GeomPoint X=155 Y=0 Z=0
  constraints (26):
    c: Vertical(g0,g1)
    c: Vertical(g4,g5)
    c: Vertical(g6,g7)
    c: Vertical(g3,g2)
    c: Horizontal(g1,g2)
    c: Horizontal(g5,g7)
    c: Horizontal(g4,g6)
    c: Horizontal(g3,g0)
    c: DistanceY(g1,g0) = 65
    c: DistanceY(g-1,g1) = 5.5
    c: DistanceX(g1,g5) = 12
    c: DistanceY(g1,g5) = 10
    c: DistanceY(g4,g0) = 10
    c: DistanceX(g7,g2) = 12
    c: DistanceX(g-1,g1) = 9
    c: PointOnObject(g8,g-1)
    c: DistanceX(g-1,g8) = 155
    c: DistanceX(g2,g8) = 9
    c: Radius(g0) = 1.9
    c: Radius(g4) = 1.9
    c: Radius(g5) = 1.9
    c: Radius(g1) = 1.9
    c: Radius(g3) = 1.9
    c: Radius(g6) = 1.9
    c: Radius(g7) = 1.9
    c: Radius(g2) = 1.9
FEATURE [PartDesign::Pocket] Pocket036
  BaseFeature = -> Chamfer027
  Length = 5
  Length2 = 100
  Profile = -> Sketch047
  Reversed = true
  Type = 1
FEATURE [Sketcher::SketchObject] Sketch048
  FullyConstrained = true
  MapMode = 5
  Placement = pos=(0,0,3) rot=(0,0,1;0rad)
  Support = -> [Pocket036]
  expr: Constraints[17] = <<args>>.pixel_w
  expr: Constraints[21] = (<<args>>.pixel_h - 45) / 2
  sketch-geometry (9):
    g0: Circle CenterX=21 CenterY=60.5 CenterZ=0 NormalX=0 NormalY=0 NormalZ=1 AngleXU=0 Radius=6
    g1: Circle CenterX=21 CenterY=60.5 CenterZ=0 NormalX=0 NormalY=0 NormalZ=1 AngleXU=0 Radius=1.9
    g2: Circle CenterX=21 CenterY=15.5 CenterZ=0 NormalX=0 NormalY=0 NormalZ=1 AngleXU=0 Radius=6
    g3: Circle CenterX=21 CenterY=15.5 CenterZ=0 NormalX=0 NormalY=0 NormalZ=1 AngleXU=0 Radius=1.9
    g4: Circle CenterX=134 CenterY=60.5 CenterZ=0 NormalX=0 NormalY=0 NormalZ=1 AngleXU=0 Radius=6
    g5: Circle CenterX=134 CenterY=60.5 CenterZ=0 NormalX=0 NormalY=0 NormalZ=1 AngleXU=0 Radius=1.9
    g6: Circle CenterX=134 CenterY=15.5 CenterZ=0 NormalX=0 NormalY=0 NormalZ=1 AngleXU=0 Radius=6
    g7: Circle CenterX=134 CenterY=15.5 CenterZ=0 NormalX=0 NormalY=0 NormalZ=1 AngleXU=0 Radius=1.9
    g8: GeomPoint X=155 Y=0 Z=0
  constraints (22):
    c: Coincident(g1,g0)
    c: Coincident(g3,g2)
    c: Coincident(g5,g4)
    c: Coincident(g7,g6)
    c: Horizontal(g2,g6)
    c: Horizontal(g0,g4)
    c: Vertical(g0,g2)
    c: Vertical(g4,g6)
    c: Radius(g1) = 1.9
    c: Radius(g3) = 1.9
    c: Radius(g5) = 1.9
    c: Radius(g7) = 1.9
    c: Radius(g0) = 6
    c: Radius(g2) = 6
    c: Radius(g6) = 6
    c: Radius(g4) = 6
    c: PointOnObject(g8,g-1)
    c: DistanceX(g-1,g8) = 155
    c: DistanceX(g-1,g2) = 21
    c: DistanceX(g6,g8) = 21
    c: DistanceY(g2,g0) = 45
    c: DistanceY(g-1,g2) = 15.5
FEATURE [PartDesign::Pad] Pad010
  BaseFeature = -> Pocket036
  Direction = (1,1,1)
  Length = 3
  Length2 = 100
  Profile = -> Sketch048
  Type = 0
FEATURE [PartDesign::Chamfer] Chamfer029
  Angle = 45
  Base = -> Pad010 [Edge93,Edge92,Edge121,Edge123,Edge95,Edge94,Edge81,Edge80,Edge122,Edge251]
  BaseFeature = -> Pad010
  ChamferType = 0
  FlipDirection = false
  Size = 0.6
  Size2 = 1
  SupportTransform = false
FEATURE [Part::Feature] Cut001005001  label="fan-air-channel001"
  Placement = pos=(-10,0,-8) rot=(0,0,1;0rad)
FEATURE [Part::Feature] Body002001  label="back001"
  Placement = pos=(0,0,-8) rot=(0,0,1;0rad)
FEATURE [Part::Cut] Cut001005002
  Base = -> Body002001
  Tool = -> Cut001005001
FEATURE [Sketcher::SketchObject] Sketch049
  FullyConstrained = true
  MapMode = 5
  Support = -> [XY_Plane004]
  sketch-geometry (23):
    g0: Circle CenterX=0 CenterY=22.5 CenterZ=0 NormalX=0 NormalY=0 NormalZ=1 AngleXU=0 Radius=1.65
    g1: Circle CenterX=0 CenterY=-22.5 CenterZ=0 NormalX=0 NormalY=0 NormalZ=1 AngleXU=0 Radius=1.65
    g2: Circle CenterX=12 CenterY=32.5 CenterZ=0 NormalX=0 NormalY=0 NormalZ=1 AngleXU=0 Radius=1.65
    g3: Circle CenterX=12 CenterY=-32.5 CenterZ=0 NormalX=0 NormalY=0 NormalZ=1 AngleXU=0 Radius=1.65
    g4: Circle CenterX=-2 CenterY=42.5 CenterZ=0 NormalX=0 NormalY=0 NormalZ=1 AngleXU=0 Radius=1.9
    g5: Circle CenterX=-2 CenterY=-12.5 CenterZ=0 NormalX=0 NormalY=0 NormalZ=1 AngleXU=0 Radius=1.9
    g6: ArcOfCircle CenterX=12 CenterY=32.5 CenterZ=0 NormalX=0 NormalY=0 NormalZ=1 AngleXU=0 Radius=5 StartAngle=0 EndAngle=1.5708
    g7: ArcOfCircle CenterX=12 CenterY=-32.5 CenterZ=0 NormalX=0 NormalY=0 NormalZ=1 AngleXU=0 Radius=5 StartAngle=3.14159 EndAngle=6.28319
    g8: LineSegment StartX=17 StartY=32.5 StartZ=0 EndX=17 EndY=-32.5 EndZ=0
    g9: LineSegment StartX=-11 StartY=46.8 StartZ=0 EndX=7 EndY=46.8 EndZ=0
    g10: LineSegment StartX=7 StartY=46.8 StartZ=0 EndX=7 EndY=37.5 EndZ=0
    g11: LineSegment StartX=7 StartY=37.5 StartZ=0 EndX=12 EndY=37.5 EndZ=0
    g12: LineSegment StartX=-11 StartY=-27.5 StartZ=0 EndX=7 EndY=-27.5 EndZ=0
    g13: LineSegment StartX=7 StartY=-27.5 StartZ=0 EndX=7 EndY=-32.5 EndZ=0
    g14: LineSegment StartX=-11 StartY=-27.5 StartZ=0 EndX=-11 EndY=46.8 EndZ=0
    g15: LineSegment StartX=-6 StartY=17.5 StartZ=0 EndX=7 EndY=17.5 EndZ=0
    g16: LineSegment StartX=7 StartY=17.5 StartZ=0 EndX=7 EndY=27.5 EndZ=0
    g17: LineSegment StartX=7 StartY=27.5 StartZ=0 EndX=12 EndY=27.5 EndZ=0
    g18: LineSegment StartX=12 StartY=27.5 StartZ=0 EndX=12 EndY=-22.5 EndZ=0
    g19: LineSegment StartX=12 StartY=-22.5 StartZ=0 EndX=7 EndY=-22.5 EndZ=0
    g20: LineSegment StartX=7 StartY=-22.5 StartZ=0 EndX=7 EndY=-7.5 EndZ=0
    g21: LineSegment StartX=7 StartY=-7.5 StartZ=0 EndX=-6 EndY=-7.5 EndZ=0
    g22: LineSegment StartX=-6 StartY=-7.5 StartZ=0 EndX=-6 EndY=17.5 EndZ=0
  constraints (69):
    c: PointOnObject(g0,g-2)
    c: PointOnObject(g1,g-2)
    c: DistanceY(g1,g0) = 45
    c: DistanceY(g1,g-1) = 22.5
    c: Vertical(g2,g3)
    c: DistanceY(g3,g2) = 65
    c: DistanceX(g1,g3) = 12
    c: DistanceY(g0,g2) = 10
    c: Radius(g0) = 1.65
    c: Radius(g1) = 1.65
    c: Radius(g2) = 1.65
    c: Radius(g3) = 1.65
    c: DistanceY(g5,g4) = 55
    c: Radius(g4) = 1.9
    c: Radius(g5) = 1.9
    c: DistanceY(g0,g4) = 20
    c: Coincident(g6,g2)
    c: Coincident(g7,g3)
    c: Horizontal(g3,g7)
    c: Horizontal(g2,g6)
    c: Radius(g6) = 5
    c: Radius(g7) = 5
    c: Horizontal(g7,g3)
    c: Coincident(g8,g6)
    c: Coincident(g8,g7)
    c: Horizontal(g9)
    c: DistanceX(g4,g9) = 9
    c: DistanceX(g9,g4) = 9
    c: DistanceY(g4,g9) = 4.3
    c: Coincident(g9,g10)
    c: Vertical(g10)
    c: Coincident(g10,g11)
    c: Coincident(g11,g6)
    c: Vertical(g2,g6)
    c: Horizontal(g11)
    c: Horizontal(g12)
    c: DistanceY(g12,g1) = 5
    c: Coincident(g13,g12)
    c: Coincident(g13,g7)
    c: Vertical(g13)
    c: Coincident(g14,g12)
    c: Coincident(g14,g9)
    c: Horizontal(g15)
    c: Coincident(g15,g16)
    c: Vertical(g16)
    c: Coincident(g16,g17)
    c: Horizontal(g17)
    c: Coincident(g17,g18)
    c: Vertical(g18)
    c: Coincident(g18,g19)
    c: Horizontal(g19)
    c: Coincident(g19,g20)
    c: Vertical(g20)
    c: Coincident(g20,g21)
    c: Horizontal(g21)
    c: Coincident(g21,g22)
    c: Coincident(g22,g15)
    c: Vertical(g22)
    c: DistanceY(g15,g0) = 5
    c: DistanceY(g5,g21) = 5
    c: DistanceX(g3,g18) = 0
    c: Horizontal(g1,g19)
    c: DistanceY(g17,g2) = 5
    c: Vertical(g14)
    c: DistanceX(g4,g0) = 2
    c: Vertical(g5,g4)
    c: DistanceX(g5,g19) = 9
    c: DistanceX(g4,g15) = 9
    c: DistanceX(g15,g4) = 4
FEATURE [PartDesign::Pad] Pad011
  Direction = (1,1,1)
  Length = 10
  Length2 = 100
  Profile = -> Sketch049
  Type = 0
FEATURE [Sketcher::SketchObject] Sketch050
  FullyConstrained = true
  MapMode = 5
  Placement = pos=(0,0,10) rot=(0,0,1;0rad)
  Support = -> [Pad011]
  sketch-geometry (4):
    g0: Circle CenterX=0 CenterY=22.5 CenterZ=0 NormalX=0 NormalY=0 NormalZ=1 AngleXU=0 Radius=3.2
    g1: Circle CenterX=0 CenterY=-22.5 CenterZ=0 NormalX=0 NormalY=0 NormalZ=1 AngleXU=0 Radius=3.2
    g2: Circle CenterX=12 CenterY=-32.5 CenterZ=0 NormalX=0 NormalY=0 NormalZ=1 AngleXU=0 Radius=3.2
    g3: Circle CenterX=12 CenterY=32.5 CenterZ=0 NormalX=0 NormalY=0 NormalZ=1 AngleXU=0 Radius=3.2
  constraints (12):
    c: PointOnObject(g0,g-2)
    c: PointOnObject(g1,g-2)
    c: Vertical(g3,g2)
    c: Radius(g3) = 3.2
    c: Radius(g2) = 3.2
    c: Radius(g1) = 3.2
    c: Radius(g0) = 3.2
    c: DistanceY(g2,g3) = 65
    c: DistanceY(g2,g-1) = 32.5
    c: DistanceY(g1,g0) = 45
    c: DistanceY(g2,g1) = 10
    c: DistanceX(g1,g2) = 12
FEATURE [PartDesign::Pocket] Pocket037
  BaseFeature = -> Pad011
  Length = 3
  Length2 = 100
  Profile = -> Sketch050
  Type = 0
FEATURE [PartDesign::Fillet] Fillet013
  Base = -> Pocket037 [Edge56,Edge57,Edge58,Edge59,Edge60,Edge61,Edge62,Edge63]
  BaseFeature = -> Pocket037
  Radius = 2
  SupportTransform = false
FEATURE [PartDesign::Fillet] Fillet014
  Base = -> Fillet013 [Edge79,Edge64,Edge77]
  BaseFeature = -> Fillet013
  Radius = 6
  SupportTransform = false
FEATURE [PartDesign::Chamfer] Chamfer030
  Angle = 45
  Base = -> Fillet014 [Face1,Edge94,Edge92]
  BaseFeature = -> Fillet014
  ChamferType = 0
  FlipDirection = false
  Size = 0.4
  Size2 = 1
  SupportTransform = false
FEATURE [PartDesign::Body] Body004016  label="spacer"
  Group = -> [Sketch049,Pad011,Sketch050,Pocket037,Fillet013,Fillet014,Chamfer030]
  Origin = -> Origin004
  Tip = -> Chamfer030
FEATURE [Part::Cylinder] Cylinder
  Angle = 360
  AttacherType = Attacher::AttachEngine3D
  Height = 10
  Placement = pos=(0,36.5,0) rot=(0,0,1;0rad)
  Radius = 1.65
FEATURE [Part::Cylinder] Cylinder001
  Angle = 360
  AttacherType = Attacher::AttachEngine3D
  Height = 10
  Placement = pos=(0,-18.5,0) rot=(0,0,1;0rad)
  Radius = 1.65
FEATURE [Part::Box] Box014  label="Cube014"
  AttacherType = Attacher::AttachEngine3D
  Height = 6.6
  Length = 18
  Placement = pos=(-9,-32.5,0) rot=(0,0,1;0rad)
  Width = 16
FEATURE [Part::Box] Box015  label="Cube015"
  AttacherType = Attacher::AttachEngine3D
  Height = 7
  Length = 18
  Placement = pos=(-9,-32.5,6) rot=(0,0,1;0rad)
  Width = 8
FEATURE [Part::Feature] Common_cs
FEATURE [Part::Cylinder] Cylinder002
  Angle = 360
  AttacherType = Attacher::AttachEngine3D
  Height = 19
  Placement = pos=(0,-26.5,9) rot=(1,0,0;1.5708rad)
  Radius = 1.9
FEATURE [Part::Cylinder] Cylinder003
  Angle = 360
  AttacherType = Attacher::AttachEngine3D
  Height = 10
  Placement = pos=(0,-18.5,0) rot=(0,0,1;0rad)
  Radius = 3.5
FEATURE [Part::Cylinder] Cylinder004
  Angle = 360
  AttacherType = Attacher::AttachEngine3D
  Height = 10
  Placement = pos=(0,36.5,0) rot=(0,0,1;0rad)
  Radius = 3.5
FEATURE [Part::MultiFuse] Fusion010
  Placement = pos=(0,0,-1.5) rot=(0,0,1;0rad)
  Shapes = -> [Cylinder001,Cylinder]
FEATURE [Part::MultiFuse] Fusion011
  Placement = pos=(0,0,3.5) rot=(0,0,1;0rad)
  Shapes = -> [Cylinder004,Cylinder003]
FEATURE [Part::MultiFuse] Fusion013
  Shapes = -> [Fusion010,Fusion011]
FEATURE [Part::Extrusion] Extrude
  Base = -> Common_cs
  Dir = (0,0,1)
  DirMode = 2
  FaceMakerClass = Part::FaceMakerBullseye
  LengthFwd = 4
  LengthRev = 0
  Solid = true
  Symmetric = false
FEATURE [Part::Cylinder] Cylinder005
  Angle = 360
  AttacherType = Attacher::AttachEngine3D
  Height = 19
  Placement = pos=(0,-16.5,9) rot=(1,0,0;1.5708rad)
  Radius = 1.45
FEATURE [Part::Fillet] Fillet015
  Base = -> Box014
  Edges = 2 edges r=6: [Edge1,Edge5]
FEATURE [Part::Fillet] Fillet016
  Base = -> Box015
  Edges = 2 edges r=6: [Edge1,Edge5]
FEATURE [Part::Fillet] Fillet017
  Base = -> Fillet016
  Edges = 2 edges r=1: [Edge4,Edge13]
FEATURE [Part::MultiFuse] Fusion017
  Shapes = -> [Fillet017,Fillet015]
FEATURE [Part::Chamfer] Chamfer031
  Base = -> Fusion017
  Edges = 5 edges r=0.4: [Edge26,Edge38,Edge42,Edge43,Edge44]
FEATURE [Part::MultiFuse] Fusion018
  Shapes = -> [Chamfer031,Body004012,Extrude]
FEATURE [Part::Cut] Cut001005003
  Base = -> Fusion018
  Tool = -> Fusion013
FEATURE [Part::MultiFuse] Fusion019
  Shapes = -> [Cylinder005,Cylinder002]
FEATURE [Part::Cut] Cut001005004
  Base = -> Cut001005003
  Refine = true
  Tool = -> Fusion019
FEATURE [Part::Chamfer] Chamfer032  label="din-clip"
  Base = -> Cut001005004
  Edges = 3 edges r=0.4: [Edge379,Edge396,Edge398]
FEATURE [Sketcher::SketchObject] Sketch051
  FullyConstrained = true
  MapMode = 5
  Support = -> [XY_Plane005]
  sketch-geometry (14):
    g0: Circle CenterX=0 CenterY=0 CenterZ=0 NormalX=0 NormalY=0 NormalZ=1 AngleXU=0 Radius=1.65
    g1: Circle CenterX=0 CenterY=45 CenterZ=0 NormalX=0 NormalY=0 NormalZ=1 AngleXU=0 Radius=1.65
    g2: Circle CenterX=12 CenterY=55.7 CenterZ=0 NormalX=0 NormalY=0 NormalZ=1 AngleXU=0 Radius=1.65
    g3: Circle CenterX=12 CenterY=2.85 CenterZ=0 NormalX=0 NormalY=0 NormalZ=1 AngleXU=0 Radius=1.65
    g4: Circle CenterX=-12 CenterY=-10 CenterZ=0 NormalX=0 NormalY=0 NormalZ=1 AngleXU=0 Radius=1.65
    g5: Circle CenterX=-12 CenterY=55 CenterZ=0 NormalX=0 NormalY=0 NormalZ=1 AngleXU=0 Radius=1.65
    g6: LineSegment StartX=21 StartY=60 StartZ=0 EndX=21 EndY=-3.65 EndZ=0
    g7: LineSegment StartX=21 StartY=-3.65 StartZ=0 EndX=3 EndY=-3.65 EndZ=0
    g8: LineSegment StartX=-7 StartY=-15 StartZ=0 EndX=-17 EndY=-15 EndZ=0
    g9: LineSegment StartX=-17 StartY=-15 StartZ=0 EndX=-17 EndY=60 EndZ=0
    g10: LineSegment StartX=-17 StartY=60 StartZ=0 EndX=-7 EndY=60 EndZ=0
    g11: LineSegment StartX=-7 StartY=-15 StartZ=0 EndX=3 EndY=-3.65 EndZ=0
    g12: LineSegment StartX=21 StartY=60 StartZ=0 EndX=3 EndY=60 EndZ=0
    g13: LineSegment StartX=3 StartY=60 StartZ=0 EndX=-7 EndY=60 EndZ=0
  constraints (41):
    c: Coincident(g0,g-1)
    c: PointOnObject(g1,g-2)
    c: DistanceY(g0,g1) = 45
    c: Vertical(g3,g2)
    c: DistanceX(g0,g3) = 12
    c: Vertical(g5,g4)
    c: DistanceX(g5,g1) = 12
    c: DistanceY(g1,g5) = 10
    c: DistanceY(g4,g0) = 10
    c: DistanceY(g3,g2) = 52.85
    c: DistanceY(g3,g0) = -2.85
    c: Equal(g1,g5)
    c: Radius(g5) = 1.65
    c: Vertical(g6)
    c: Coincident(g6,g7)
    c: Horizontal(g7)
    c: Coincident(g8,g9)
    c: Vertical(g9)
    c: Coincident(g9,g10)
    c: Horizontal(g10)
    c: Horizontal(g8)
    c: DistanceX(g7,g3) = 9
    c: DistanceX(g3,g6) = 9
    c: DistanceX(g5,g10) = 5
    c: DistanceY(g5,g10) = 5
    c: DistanceX(g9,g5) = 5
    c: DistanceY(g8,g4) = 5
    c: DistanceX(g4,g8) = 5
    c: Coincident(g11,g7)
    c: Coincident(g11,g8)
    c: Equal(g4,g0)
    c: Equal(g0,g1)
    c: Equal(g3,g2)
    c: Radius(g2) = 1.65
    c: DistanceY(g2,g6) = 4.3
    c: Coincident(g6,g12)
    c: Horizontal(g12)
    c: Coincident(g12,g13)
    c: Coincident(g13,g10)
    c: DistanceX(g12,g2) = 9
    c: DistanceY(g7,g0) = 3.65
FEATURE [PartDesign::Pad] Pad012
  Direction = (1,1,1)
  Length = 10
  Length2 = 100
  Profile = -> Sketch051
  Type = 0
FEATURE [Sketcher::SketchObject] Sketch053
  FullyConstrained = true
  MapMode = 5
  Placement = pos=(0,0,3) rot=(0,0,1;0rad)
  Support = -> [Chamfer029]
  sketch-geometry (20):
    g0: ArcOfCircle CenterX=19 CenterY=44 CenterZ=0 NormalX=0 NormalY=0 NormalZ=1 AngleXU=0 Radius=2 StartAngle=1.5708 EndAngle=4.71239
    g1: ArcOfCircle CenterX=34 CenterY=44 CenterZ=0 NormalX=0 NormalY=0 NormalZ=1 AngleXU=0 Radius=2 StartAngle=4.71239 EndAngle=7.85398
    g2: LineSegment StartX=19 StartY=42 StartZ=0 EndX=34 EndY=42 EndZ=0
    g3: LineSegment StartX=19 StartY=46 StartZ=0 EndX=34 EndY=46 EndZ=0
    g4: ArcOfCircle CenterX=19 CenterY=38 CenterZ=0 NormalX=0 NormalY=0 NormalZ=1 AngleXU=0 Radius=2 StartAngle=1.5708 EndAngle=4.71239
    g5: ArcOfCircle CenterX=34 CenterY=38 CenterZ=0 NormalX=0 NormalY=0 NormalZ=1 AngleXU=0 Radius=2 StartAngle=4.71239 EndAngle=7.85398
    g6: LineSegment StartX=19 StartY=36 StartZ=0 EndX=34 EndY=36 EndZ=0
    g7: LineSegment StartX=19 StartY=40 StartZ=0 EndX=34 EndY=40 EndZ=0
    g8: ArcOfCircle CenterX=19 CenterY=32 CenterZ=0 NormalX=0 NormalY=0 NormalZ=1 AngleXU=0 Radius=2 StartAngle=1.5708 EndAngle=4.71239
    g9: ArcOfCircle CenterX=34 CenterY=32 CenterZ=0 NormalX=0 NormalY=0 NormalZ=1 AngleXU=0 Radius=2 StartAngle=4.71239 EndAngle=7.85398
    g10: LineSegment StartX=19 StartY=30 StartZ=0 EndX=34 EndY=30 EndZ=0
    g11: LineSegment StartX=19 StartY=34 StartZ=0 EndX=34 EndY=34 EndZ=0
    g12: ArcOfCircle CenterX=19 CenterY=26 CenterZ=0 NormalX=0 NormalY=0 NormalZ=1 AngleXU=0 Radius=2 StartAngle=1.5708 EndAngle=4.71239
    g13: ArcOfCircle CenterX=34 CenterY=26 CenterZ=0 NormalX=0 NormalY=0 NormalZ=1 AngleXU=0 Radius=2 StartAngle=4.71239 EndAngle=7.85398
    g14: LineSegment StartX=19 StartY=24 StartZ=0 EndX=34 EndY=24 EndZ=0
    g15: LineSegment StartX=19 StartY=28 StartZ=0 EndX=34 EndY=28 EndZ=0
    g16: ArcOfCircle CenterX=19 CenterY=50 CenterZ=0 NormalX=0 NormalY=0 NormalZ=1 AngleXU=0 Radius=2 StartAngle=1.5708 EndAngle=4.71239
    g17: ArcOfCircle CenterX=34 CenterY=50 CenterZ=0 NormalX=0 NormalY=0 NormalZ=1 AngleXU=0 Radius=2 StartAngle=4.71239 EndAngle=7.85398
    g18: LineSegment StartX=19 StartY=48 StartZ=0 EndX=34 EndY=48 EndZ=0
    g19: LineSegment StartX=19 StartY=52 StartZ=0 EndX=34 EndY=52 EndZ=0
  constraints (50):
    c: Tangent(g0,g3) = 1.5708
    c: Tangent(g0,g2) = -1.5708
    c: Tangent(g2,g1) = -1.5708
    c: Tangent(g3,g1) = 1.5708
    c: Horizontal(g2)
    c: Equal(g0,g1)
    c: Tangent(g4,g7) = 1.5708
    c: Tangent(g4,g6) = -1.5708
    c: Tangent(g6,g5) = -1.5708
    c: Tangent(g7,g5) = 1.5708
    c: Horizontal(g6)
    c: Equal(g4,g5)
    c: Tangent(g8,g11) = 1.5708
    c: Tangent(g8,g10) = -1.5708
    c: Tangent(g10,g9) = -1.5708
    c: Tangent(g11,g9) = 1.5708
    c: Horizontal(g10)
    c: Equal(g8,g9)
    c: Vertical(g8,g4)
    c: Vertical(g4,g0)
    c: Vertical(g9,g5)
    c: Vertical(g5,g1)
    c: Equal(g0,g4)
    c: Equal(g4,g8)
    c: Radius(g0) = 2
    c: DistanceY(g4,g0) = 2
    c: DistanceY(g8,g4) = 2
    c: Tangent(g12,g15) = 1.5708
    c: Tangent(g12,g14) = -1.5708
    c: Tangent(g14,g13) = -1.5708
    c: Tangent(g15,g13) = 1.5708
    c: Horizontal(g14)
    c: Equal(g12,g13)
    c: Equal(g12,g8)
    c: Vertical(g12,g8)
    c: Vertical(g13,g9)
    c: DistanceY(g12,g8) = 2
    c: DistanceX(g0,g1) = 15
    c: DistanceX(g-1,g12) = 19
    c: DistanceY(g-1,g12) = 26
    c: Tangent(g16,g19) = 1.5708
    c: Tangent(g16,g18) = -1.5708
    c: Tangent(g18,g17) = -1.5708
    c: Tangent(g19,g17) = 1.5708
    c: Horizontal(g18)
    c: Equal(g16,g17)
    c: Equal(g0,g16)
    c: Vertical(g16,g0)
    c: DistanceY(g0,g16) = 2
    c: Vertical(g17,g1)
FEATURE [PartDesign::Pocket] Pocket040  label="cooling-fin-hole"
  BaseFeature = -> Chamfer029
  Length = 5
  Length2 = 100
  Profile = -> Sketch053
  Type = 1
FEATURE [PartDesign::Chamfer] Chamfer034
  Angle = 45
  Base = -> Pocket040 [Edge200,Edge55,Edge192,Edge51,Edge156,Face36,Edge148,Face32,Edge140,Face28,Edge27]
  BaseFeature = -> Pocket040
  ChamferType = 0
  FlipDirection = false
  Size = 0.4
  Size2 = 1
  SupportTransform = false
FEATURE [Part::Feature] Defeatured  label="din-base"
FEATURE [PartDesign::FeatureBase] BaseFeature
  BaseFeature = -> Defeatured
FEATURE [PartDesign::Pad] Pad013
  BaseFeature = -> BaseFeature
  Direction = (1,1,1)
  Length = 5
  Length2 = 100
  Profile = -> BaseFeature [Face129]
  Type = 0
FEATURE [PartDesign::Pad] Pad014
  BaseFeature = -> Pad013
  Direction = (1,1,1)
  Length = 7
  Length2 = 100
  Profile = -> Pad013 [Face74]
  Refine = true
  Type = 0
FEATURE [Sketcher::SketchObject] Sketch054
  FullyConstrained = true
  MapMode = 5
  Placement = pos=(0,0,0.0031494) rot=(0,0,1;0rad)
  Support = -> [Pad014]
  sketch-geometry (2):
    g0: Circle CenterX=0 CenterY=-28.5 CenterZ=0 NormalX=0 NormalY=0 NormalZ=1 AngleXU=0 Radius=2
    g1: Circle CenterX=0 CenterY=24.3 CenterZ=0 NormalX=0 NormalY=0 NormalZ=1 AngleXU=0 Radius=2
  constraints (6):
    c: PointOnObject(g0,g-2)
    c: PointOnObject(g1,g-2)
    c: Equal(g1,g0)
    c: Radius(g0) = 2
    c: DistanceY(g-1,g1) = 24.3  '0.00 mm'
    c: DistanceY(g0,g-1) = 28.5
FEATURE [PartDesign::Pocket] Pocket041
  BaseFeature = -> Pad014
  Length = 5
  Length2 = 100
  Profile = -> Sketch054
  Type = 0
FEATURE [Sketcher::SketchObject] Sketch055
  FullyConstrained = true
  MapMode = 5
  Placement = pos=(-6.216e-13,-32.803,-6.86e-14) rot=(1,0,0;1.5708rad)
  Support = -> [Pocket041]
  sketch-geometry (1):
    g0: Circle CenterX=0 CenterY=-9 CenterZ=0 NormalX=0 NormalY=0 NormalZ=1 AngleXU=0 Radius=2
  constraints (3):
    c: PointOnObject(g0,g-2)
    c: Radius(g0) = 2
    c: DistanceY(g0,g-1) = 9
FEATURE [PartDesign::Pocket] Pocket042
  BaseFeature = -> Pocket041
  Length = 0
  Length2 = 100
  Profile = -> Sketch055
  Type = 3
  UpToFace = -> Pocket041 [Face85]
FEATURE [PartDesign::Chamfer] Chamfer035
  Angle = 45
  Base = -> Pocket042 [Face72,Face136,Edge242,Edge99,Edge15,Edge17,Edge16]
  BaseFeature = -> Pocket042
  ChamferType = 0
  FlipDirection = false
  Size = 0.4
  Size2 = 1
  SupportTransform = false
FEATURE [PartDesign::Body] Body004018  label="din-mount-type-2"
  BaseFeature = -> Defeatured
  Group = -> [BaseFeature,Pad013,Pad014,Sketch054,Pocket041,Sketch055,Pocket042,Chamfer035]
  Origin = -> Origin006
  Placement = pos=(33,42.65,-18) rot=(0,0,1;3.14159rad)
  Tip = -> Chamfer035
FEATURE [PartDesign::Fillet] Fillet018
  Base = -> Pad012 [Edge1,Edge2]
  BaseFeature = -> Pad012
  Radius = 6
  SupportTransform = false
FEATURE [PartDesign::Fillet] Fillet019
  Base = -> Fillet018 [Edge42,Edge41,Edge39,Edge37,Edge38,Edge40]
  BaseFeature = -> Fillet018
  Radius = 5
  SupportTransform = false
FEATURE [Sketcher::SketchObject] Sketch058
  FullyConstrained = true
  MapMode = 5
  Placement = pos=(0,0,0) rot=(1,0,0;3.14159rad)
  Support = -> [Chamfer034]
  sketch-geometry (5):
    g0: ArcOfCircle CenterX=75 CenterY=-62 CenterZ=0 NormalX=0 NormalY=0 NormalZ=1 AngleXU=0 Radius=2 StartAngle=1.5708 EndAngle=4.71239
    g1: ArcOfCircle CenterX=77 CenterY=-62 CenterZ=0 NormalX=0 NormalY=0 NormalZ=1 AngleXU=0 Radius=2 StartAngle=4.71239 EndAngle=7.85398
    g2: LineSegment StartX=75 StartY=-64 StartZ=0 EndX=77 EndY=-64 EndZ=0
    g3: LineSegment StartX=75 StartY=-60 StartZ=0 EndX=77 EndY=-60 EndZ=0
    g4: Circle CenterX=100 CenterY=-60 CenterZ=0 NormalX=0 NormalY=0 NormalZ=1 AngleXU=0 Radius=4
  constraints (13):
    c: Tangent(g0,g3) = 1.5708
    c: Tangent(g0,g2) = -1.5708
    c: Tangent(g2,g1) = -1.5708
    c: Tangent(g3,g1) = 1.5708
    c: Horizontal(g2)
    c: Equal(g0,g1)
    c: Radius(g1) = 2
    c: DistanceX(g0,g1) = 2
    c: DistanceX(g-1,g0) = 75
    c: DistanceY(g0,g-1) = 62
    c: Radius(g4) = 4
    c: DistanceX(g-1,g4) = 100
    c: DistanceY(g4,g-1) = 60
FEATURE [PartDesign::Pocket] Pocket045
  BaseFeature = -> Chamfer034
  Length = 5
  Length2 = 100
  Profile = -> Sketch058
  Type = 1
FEATURE [Sketcher::SketchObject] Sketch059
  FullyConstrained = true
  MapMode = 5
  Placement = pos=(0,0,0) rot=(1,0,0;3.14159rad)
  Support = -> [Pocket045]
  sketch-geometry (1):
    g0: Circle CenterX=120 CenterY=-65 CenterZ=0 NormalX=0 NormalY=0 NormalZ=1 AngleXU=0 Radius=5
  constraints (3):
    c: Radius(g0) = 5
    c: DistanceX(g-1,g0) = 120
    c: DistanceY(g0,g-1) = 65
FEATURE [PartDesign::Pad] Pad015
  BaseFeature = -> Pocket045
  Direction = (1,1,1)
  Length = 10
  Length2 = 100
  Profile = -> Sketch059
  Refine = true
  Type = 3
  UpToFace = -> Pocket045 [Face111]
FEATURE [PartDesign::Chamfer] Chamfer036002
  Angle = 45
  Base = -> Pad015 [Edge317,Edge449,Edge313,Edge447]
  BaseFeature = -> Pad015
  ChamferType = 0
  FlipDirection = false
  Size = 0.4
  Size2 = 1
  SupportTransform = false
FEATURE [PartDesign::Chamfer] Chamfer036003
  Angle = 45
  Base = -> Chamfer036002 [Edge69,Edge68,Edge66,Edge67,Edge207,Edge203,Edge202,Edge206,Edge59,Edge189]
  BaseFeature = -> Chamfer036002
  ChamferType = 0
  FlipDirection = false
  Size = 0.4
  Size2 = 1
  SupportTransform = false
FEATURE [PartDesign::Body] Body002  label="back"
  Group = -> [DatumPlane006,Sketch011,Pad001,DatumPlane007,Sketch012,Pocket009,DatumPlane009,DatumPlane010,DatumPlane011,DatumPlane012,Sketch013,Pad002,Sketch014,Pad003,Sketch016,Pocket011,Sketch017,Pocket012,Sketch020,Pocket015,Sketch021,Pad004,Sketch023,Pocket017,Sketch024,Pad005,Fillet006,Chamfer006,Fillet007,Sketch025,Pad006,Sketch028,Pocket020,Sketch029,Pocket021,Sketch040,Pad009,Sketch041,Pocket030,+20 more]
  Origin = -> Origin001
  Placement = pos=(0,0,-8) rot=(0,0,1;0rad)
  Tip = -> Chamfer036003
  expr: .Placement.Base.z = -<<args>>.back_thickness
FEATURE [Sketcher::SketchObject] Sketch060
  FullyConstrained = true
  MapMode = 5
  Support = -> [XY_Plane007]
  sketch-geometry (4):
    g0: LineSegment StartX=-20 StartY=20 StartZ=0 EndX=20 EndY=20 EndZ=0
    g1: LineSegment StartX=20 StartY=20 StartZ=0 EndX=20 EndY=-20 EndZ=0
    g2: LineSegment StartX=20 StartY=-20 StartZ=0 EndX=-20 EndY=-20 EndZ=0
    g3: LineSegment StartX=-20 StartY=-20 StartZ=0 EndX=-20 EndY=20 EndZ=0
  constraints (12):
    c: Coincident(g0,g1)
    c: Coincident(g1,g2)
    c: Coincident(g2,g3)
    c: Coincident(g3,g0)
    c: Horizontal(g0)
    c: Horizontal(g2)
    c: Vertical(g1)
    c: Vertical(g3)
    c: DistanceX(g0,g0) = 40
    c: DistanceX(g0,g-1) = 20
    c: DistanceY(g3,g3) = 40
    c: DistanceY(g-1,g0) = 20
FEATURE [PartDesign::Pad] Pad016
  Direction = (1,1,1)
  Length = 3
  Length2 = 100
  Profile = -> Sketch060
  Type = 0
FEATURE [Sketcher::SketchObject] Sketch061
  FullyConstrained = true
  MapMode = 5
  Placement = pos=(0,0,0) rot=(1,0,0;3.14159rad)
  Support = -> [Pad016]
  sketch-geometry (4):
    g0: Circle CenterX=-16 CenterY=16 CenterZ=0 NormalX=0 NormalY=0 NormalZ=1 AngleXU=0 Radius=2.25
    g1: Circle CenterX=-16 CenterY=-16 CenterZ=0 NormalX=0 NormalY=0 NormalZ=1 AngleXU=0 Radius=2.25
    g2: Circle CenterX=16 CenterY=-16 CenterZ=0 NormalX=0 NormalY=0 NormalZ=1 AngleXU=0 Radius=2.25
    g3: Circle CenterX=16 CenterY=16 CenterZ=0 NormalX=0 NormalY=0 NormalZ=1 AngleXU=0 Radius=2.25
  constraints (12):
    c: Equal(g3,g0)
    c: Equal(g0,g1)
    c: Equal(g1,g2)
    c: Horizontal(g0,g3)
    c: Horizontal(g1,g2)
    c: Vertical(g1,g0)
    c: Vertical(g2,g3)
    c: DistanceX(g0,g-1) = 16
    c: DistanceX(g0,g3) = 32
    c: DistanceY(g-1,g3) = 16
    c: DistanceY(g2,g3) = 32
    c: Radius(g0) = 2.25
FEATURE [PartDesign::Pad] Pad017
  BaseFeature = -> Pad016
  Direction = (1,1,1)
  Length = 2.5
  Length2 = 100
  Profile = -> Sketch061
  Type = 0
FEATURE [Sketcher::SketchObject] Sketch062
  FullyConstrained = true
  MapMode = 5
  Placement = pos=(0,0,0) rot=(1,0,0;3.14159rad)
  Support = -> [Pad017]
  sketch-geometry (1):
    g0: Circle CenterX=0 CenterY=0 CenterZ=0 NormalX=0 NormalY=0 NormalZ=1 AngleXU=0 Radius=19.25
  constraints (2):
    c: Coincident(g0,g-1)
    c: Radius(g0) = 19.25
FEATURE [PartDesign::Pocket] Pocket046
  BaseFeature = -> Pad017
  Length = 1.5
  Length2 = 100
  Profile = -> Sketch062
  Type = 0
FEATURE [Sketcher::SketchObject] Sketch063
  FullyConstrained = true
  MapMode = 5
  Placement = pos=(0,0,-2.5) rot=(1,0,0;3.14159rad)
  Support = -> [Pocket046]
  sketch-geometry (4):
    g0: Circle CenterX=-16 CenterY=16 CenterZ=0 NormalX=0 NormalY=0 NormalZ=1 AngleXU=0 Radius=1.65
    g1: Circle CenterX=-16 CenterY=-16 CenterZ=0 NormalX=0 NormalY=0 NormalZ=1 AngleXU=0 Radius=1.65
    g2: Circle CenterX=16 CenterY=-16 CenterZ=0 NormalX=0 NormalY=0 NormalZ=1 AngleXU=0 Radius=1.65
    g3: Circle CenterX=16 CenterY=16 CenterZ=0 NormalX=0 NormalY=0 NormalZ=1 AngleXU=0 Radius=1.65
  constraints (12):
    c: Horizontal(g0,g3)
    c: Horizontal(g1,g2)
    c: Vertical(g1,g0)
    c: Vertical(g3,g2)
    c: DistanceX(g0,g-1) = 16
    c: DistanceX(g0,g3) = 32
    c: DistanceY(g-1,g0) = 16
    c: DistanceY(g1,g0) = 32
    c: Radius(g0) = 1.65
    c: Equal(g0,g1)
    c: Equal(g1,g2)
    c: Equal(g2,g3)
FEATURE [PartDesign::Pocket] Pocket047
  BaseFeature = -> Pocket046
  Length = 5
  Length2 = 100
  Profile = -> Sketch063
  Type = 1
FEATURE [PartDesign::Fillet] Fillet021
  Base = -> Pocket047 [Edge1,Edge2,Edge8,Edge5]
  BaseFeature = -> Pocket047
  Radius = 3
  SupportTransform = false
FEATURE [PartDesign::Body] Body004019  label="fan-guard"
  Group = -> [Sketch060,Pad016,Sketch061,Pad017,Sketch062,Pocket046,Sketch063,Pocket047,Fillet021]
  Origin = -> Origin007
  Tip = -> Fillet021
FEATURE [Sketcher::SketchObject] Sketch064
  ExternalGeometry = -> [Fillet019]
  FullyConstrained = true
  MapMode = 5
  Placement = pos=(0,0,10) rot=(0,0,1;0rad)
  Support = -> [Fillet019]
  sketch-geometry (2):
    g0: Circle CenterX=12 CenterY=55.7 CenterZ=0 NormalX=0 NormalY=0 NormalZ=1 AngleXU=0 Radius=3.2
    g1: Circle CenterX=12 CenterY=2.85 CenterZ=0 NormalX=0 NormalY=0 NormalZ=1 AngleXU=0 Radius=3.2
  constraints (4):
    c: Coincident(g0,g-3)
    c: Coincident(g1,g-4)
    c: Equal(g1,g0)
    c: Radius(g0) = 3.2
FEATURE [PartDesign::Pocket] Pocket048
  BaseFeature = -> Fillet019
  Length = 4
  Length2 = 100
  Profile = -> Sketch064
  Type = 0
FEATURE [Sketcher::SketchObject] Sketch065
  ExternalGeometry = -> [Pocket048]
  FullyConstrained = true
  MapMode = 5
  Placement = pos=(0,0,10) rot=(0,0,1;0rad)
  Support = -> [Pocket048]
  sketch-geometry (12):
    g0: LineSegment StartX=7 StartY=51.2 StartZ=0 EndX=17 EndY=51.2 EndZ=0
    g1: LineSegment StartX=17 StartY=51.2 StartZ=0 EndX=17 EndY=7.35 EndZ=0
    g2: LineSegment StartX=17 StartY=7.35 StartZ=0 EndX=7 EndY=7.35 EndZ=0
    g3: LineSegment StartX=7 StartY=7.35 StartZ=0 EndX=7 EndY=51.2 EndZ=0
    g4: LineSegment StartX=-12 StartY=50 StartZ=0 EndX=-7 EndY=50 EndZ=0
    g5: LineSegment StartX=-7 StartY=50 StartZ=0 EndX=-5 EndY=40 EndZ=0
    g6: LineSegment StartX=-5 StartY=40 StartZ=0 EndX=3 EndY=40 EndZ=0
    g7: LineSegment StartX=3 StartY=40 StartZ=0 EndX=3 EndY=5 EndZ=0
    g8: LineSegment StartX=3 StartY=5 StartZ=0 EndX=-5 EndY=5 EndZ=0
    g9: LineSegment StartX=-5 StartY=5 StartZ=0 EndX=-7 EndY=-5 EndZ=0
    g10: LineSegment StartX=-7 StartY=-5 StartZ=0 EndX=-12 EndY=-5 EndZ=0
    g11: LineSegment StartX=-12 StartY=-5 StartZ=0 EndX=-12 EndY=50 EndZ=0
  constraints (36):
    c: Coincident(g0,g1)
    c: Coincident(g1,g2)
    c: Coincident(g2,g3)
    c: Coincident(g3,g0)
    c: Horizontal(g0)
    c: Horizontal(g2)
    c: Vertical(g1)
    c: Vertical(g3)
    c: DistanceX(g0,g0) = 10
    c: DistanceX(g0,g-3) = 5
    c: DistanceY(g0,g-3) = 4.5
    c: DistanceY(g-4,g2) = 4.5
    c: Horizontal(g4)
    c: Coincident(g4,g5)
    c: Coincident(g5,g6)
    c: Horizontal(g6)
    c: Coincident(g6,g7)
    c: Vertical(g7)
    c: Coincident(g7,g8)
    c: Horizontal(g8)
    c: Coincident(g8,g9)
    c: Coincident(g9,g10)
    c: Horizontal(g10)
    c: Coincident(g10,g11)
    c: Coincident(g11,g4)
    c: Vertical(g11)
    c: DistanceX(g-8,g4) = 5
    c: DistanceY(g4,g-5) = 5
    c: DistanceY(g-7,g10) = 5
    c: DistanceX(g6,g-3) = 9
    c: DistanceY(g6,g-6) = 5
    c: DistanceY(g-1,g7) = 5
    c: DistanceX(g5,g-6) = 5
    c: DistanceX(g8,g-1) = 5
    c: DistanceX(g10,g10) = 5
    c: DistanceX(g4,g4) = 5
FEATURE [PartDesign::Pocket] Pocket049
  BaseFeature = -> Pocket048
  Length = 5
  Length2 = 100
  Profile = -> Sketch065
  Type = 1
FEATURE [PartDesign::Fillet] Fillet022
  Base = -> Pocket049 [Edge68,Edge69,Edge81,Edge79,Edge77,Edge75,Edge73,Edge71,Edge85,Edge89,Edge87,Edge84]
  BaseFeature = -> Pocket049
  Radius = 1
  SupportTransform = false
FEATURE [Sketcher::SketchObject] Sketch066
  ExternalGeometry = -> [Fillet022]
  FullyConstrained = true
  MapMode = 5
  Placement = pos=(0,0,0) rot=(1,0,0;3.14159rad)
  Support = -> [Fillet022]
  sketch-geometry (4):
    g0: LineSegment StartX=2 StartY=-40 StartZ=0 EndX=8 EndY=-40 EndZ=0
    g1: LineSegment StartX=8 StartY=-40 StartZ=0 EndX=8 EndY=-7.35 EndZ=0
    g2: LineSegment StartX=8 StartY=-7.35 StartZ=0 EndX=2 EndY=-7.35 EndZ=0
    g3: LineSegment StartX=2 StartY=-7.35 StartZ=0 EndX=2 EndY=-40 EndZ=0
  constraints (10):
    c: Coincident(g0,g1)
    c: Coincident(g1,g2)
    c: Coincident(g2,g3)
    c: Coincident(g3,g0)
    c: Horizontal(g0)
    c: Horizontal(g2)
    c: Vertical(g1)
    c: Vertical(g3)
    c: Coincident(g0,g-5)
    c: Coincident(g1,g-3)
FEATURE [PartDesign::Pocket] Pocket050
  BaseFeature = -> Fillet022
  Length = 5
  Length2 = 100
  Profile = -> Sketch066
  Type = 1
FEATURE [PartDesign::Fillet] Fillet023
  Base = -> Pocket050 [Edge100,Edge84]
  BaseFeature = -> Pocket050
  Radius = 1
  SupportTransform = false
FEATURE [PartDesign::Chamfer] Chamfer036004
  Angle = 45
  Base = -> Fillet023 [Face1,Face48]
  BaseFeature = -> Fillet023
  ChamferType = 0
  FlipDirection = false
  Size = 0.4
  Size2 = 1
  SupportTransform = false
FEATURE [PartDesign::Body] Body004017  label="low-spacer"
  Group = -> [Sketch051,Pad012,Fillet018,Fillet019,Sketch064,Pocket048,Sketch065,Pocket049,Fillet022,Sketch066,Pocket050,Fillet023,Chamfer036004]
  Origin = -> Origin005
  Placement = pos=(21,15.5,-18) rot=(0,0,1;0rad)
  Tip = -> Chamfer036004
FEATURE [PartDesign::FeatureBase] BaseFeature001
  BaseFeature = -> Body004013
FEATURE [PartDesign::Pad] Pad018
  BaseFeature = -> BaseFeature001
  Direction = (1,1,1)
  Length = 5
  Length2 = 100
  Profile = -> BaseFeature001 [Face147]
  Refine = true
  Type = 0
FEATURE [PartDesign::Pad] Pad019
  BaseFeature = -> Pad018
  Direction = (1,1,1)
  Length = 7
  Length2 = 100
  Profile = -> Pad018 [Face146]
  Type = 0
FEATURE [PartDesign::Pad] Pad020
  BaseFeature = -> Pad019
  Direction = (1,1,1)
  Length = 10
  Length2 = 100
  Profile = -> Pad019 [Face129]
  Type = 0
FEATURE [Sketcher::SketchObject] Sketch067
  FullyConstrained = true
  MapMode = 5
  Placement = pos=(-6.233e-13,-32.803,-2.88e-14) rot=(1,0,0;1.5708rad)
  Support = -> [Pad020]
  sketch-geometry (1):
    g0: Circle CenterX=0 CenterY=-10 CenterZ=0 NormalX=0 NormalY=0 NormalZ=1 AngleXU=0 Radius=1.9
  constraints (3):
    c: PointOnObject(g0,g-2)
    c: Radius(g0) = 1.9
    c: DistanceY(g0,g-1) = 10
FEATURE [PartDesign::Pocket] Pocket051
  BaseFeature = -> Pad020
  Length = 0
  Length2 = 100
  Profile = -> Sketch067
  Refine = true
  Type = 3
  UpToFace = -> Pad020 [Face162]
FEATURE [PartDesign::Chamfer] Chamfer036005
  Angle = 45
  Base = -> Pocket051 [Face163,Face165,Face147,Edge419,Edge368]
  BaseFeature = -> Pocket051
  ChamferType = 0
  FlipDirection = false
  Size = 0.4
  Size2 = 1
  SupportTransform = false
FEATURE [Sketcher::SketchObject] Sketch068
  ExternalGeometry = -> [Chamfer036005]
  FullyConstrained = true
  MapMode = 5
  Placement = pos=(-1.774e-13,4.86e-14,-17.5969) rot=(1,0,0;3.14159rad)
  Support = -> [Chamfer036005]
  sketch-geometry (6):
    g0: LineSegment StartX=-5.00279 StartY=-20.497 StartZ=0 EndX=4.99721 EndY=-20.497 EndZ=0
    g1: LineSegment StartX=4.99721 StartY=-20.497 StartZ=0 EndX=4.99721 EndY=-24.797 EndZ=0
    g2: LineSegment StartX=4.99721 StartY=-24.797 StartZ=0 EndX=2.99721 EndY=-26.797 EndZ=0
    g3: LineSegment StartX=2.99721 StartY=-26.797 StartZ=0 EndX=-3.00279 EndY=-26.797 EndZ=0
    g4: LineSegment StartX=-3.00279 StartY=-26.797 StartZ=0 EndX=-5.00279 EndY=-24.797 EndZ=0
    g5: LineSegment StartX=-5.00279 StartY=-24.797 StartZ=0 EndX=-5.00279 EndY=-20.497 EndZ=0
  constraints (18):
    c: Horizontal(g0)
    c: Coincident(g0,g1)
    c: Vertical(g1)
    c: Coincident(g1,g2)
    c: Coincident(g2,g3)
    c: Horizontal(g3)
    c: Coincident(g3,g4)
    c: Coincident(g4,g5)
    c: Coincident(g5,g0)
    c: Vertical(g5)
    c: DistanceX(g-3,g0) = 4
    c: DistanceX(g0,g-4) = 4
    c: DistanceY(g0,g-3) = 3
    c: DistanceY(g-5,g3) = 4
    c: DistanceX(g4,g3) = 2
    c: Horizontal(g4,g1)
    c: DistanceX(g2,g1) = 2
    c: DistanceY(g3,g4) = 2
FEATURE [PartDesign::Pocket] Pocket052
  BaseFeature = -> Chamfer036005
  Length = 5
  Length2 = 100
  Profile = -> Sketch068
  Type = 1
FEATURE [PartDesign::Fillet] Fillet024
  Base = -> Pocket052 [Edge332,Edge331,Edge334,Edge336,Edge338,Edge340]
  BaseFeature = -> Pocket052
  Radius = 1
  SupportTransform = false
FEATURE [PartDesign::Chamfer] Chamfer036006
  Angle = 45
  Base = -> Fillet024 [Edge86,Edge8]
  BaseFeature = -> Fillet024
  ChamferType = 0
  FlipDirection = false
  Size = 0.4
  Size2 = 1
  SupportTransform = false
FEATURE [PartDesign::Body] Body004020
  BaseFeature = -> Body004013
  Group = -> [BaseFeature001,Pad018,Pad019,Pad020,Sketch067,Pocket051,Chamfer036005,Sketch068,Pocket052,Fillet024,Chamfer036006]
  Origin = -> Origin008
  Tip = -> Chamfer036006
